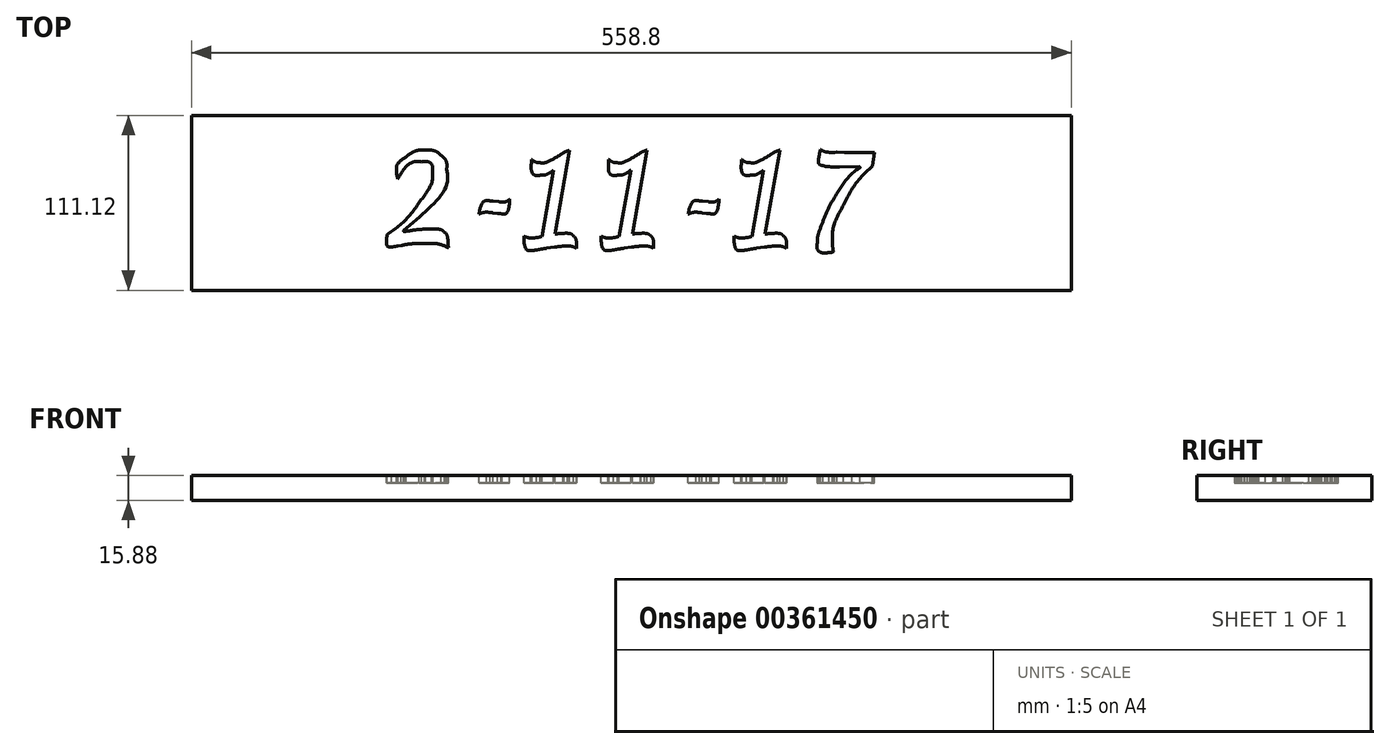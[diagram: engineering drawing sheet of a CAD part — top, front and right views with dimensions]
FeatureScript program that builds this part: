
annotation { "Feature Type Name" : "Feature", "Feature Type Description" : "" }
export const myFeature = defineFeature(function(context is Context, id is Id, definition is map)
    precondition{}
    {
        {
            var Q0;
            Q0=qCreatedBy(makeId("Top.planeOp"),FACE);
            var sketch = newSketch(context, id + "F0", { "sketchPlane" : qUnion([Q0])});
            skLineSegment(sketch, "E0.bottom", {"start": v(12.7, 0) * mm, "end": v(546.1, 0) * mm});
            skLineSegment(sketch, "E0.top", {"start": v(12.7, 609.6) * mm, "end": v(546.1, 609.6) * mm});
            skLineSegment(sketch, "E0.left", {"start": v(0, 12.7) * mm, "end": v(0, 596.9) * mm});
            skLineSegment(sketch, "E0.right", {"start": v(558.8, 12.7) * mm, "end": v(558.8, 596.9) * mm});
            skPoint(sketch, "E1.visualSharp", {"position": v(0, 609.6) * mm});
            skArc(sketch, "E1.filletArc", {"start": v(12.7, 609.6) * mm, "mid": v(3.72, 605.88) * mm, "end": v(0, 596.9) * mm});
            skPoint(sketch, "E2.visualSharp", {"position": v(0, 0) * mm});
            skArc(sketch, "E2.filletArc", {"start": v(0, 12.7) * mm, "mid": v(3.72, 3.72) * mm, "end": v(12.7, 0) * mm});
            skPoint(sketch, "E3.visualSharp", {"position": v(558.8, 0) * mm});
            skArc(sketch, "E3.filletArc", {"start": v(546.1, 0) * mm, "mid": v(555.08, 3.72) * mm, "end": v(558.8, 12.7) * mm});
            skPoint(sketch, "E4.visualSharp", {"position": v(558.8, 609.6) * mm});
            skArc(sketch, "E4.filletArc", {"start": v(558.8, 596.9) * mm, "mid": v(555.08, 605.88) * mm, "end": v(546.1, 609.6) * mm});
            skSolve(sketch);
        }
        {
            var Q0;
            Q0=makeQuery(id+"F0.imprint","IMPRINT",FACE,{"disambiguationData":[TD([[makeQuery(id+"F0.imprint","IMPRINT",EDGE,{"derivedFrom":sQuery(id+"F0.wireOp",EDGE,"E0.bottom")}),1.0]])]});
            extrude(context, id + "F1", {"entities" : qUnion([Q0]), "depth" : 15.88 * mm});
        }
        {
            var Q0;
            Q0=makeQuery(id+"F1.opExtrude","CAP_FACE",FACE,{"disambiguationData":[OSD([sQuery(id+"F0.wireOp",EDGE,"E0.bottom"),sQuery(id+"F0.wireOp",EDGE,"E0.top"),sQuery(id+"F0.wireOp",EDGE,"E0.left"),sQuery(id+"F0.wireOp",EDGE,"E0.right"),sQuery(id+"F0.wireOp",EDGE,"E1.filletArc"),sQuery(id+"F0.wireOp",EDGE,"E2.filletArc"),sQuery(id+"F0.wireOp",EDGE,"E3.filletArc"),sQuery(id+"F0.wireOp",EDGE,"E4.filletArc")])],"isStart":false});
            var sketch = newSketch(context, id + "F2", { "sketchPlane" : qUnion([Q0])});
            skFitSpline(sketch, "E5", {"points": [v(247.46, 485.02) * mm, v(244.22, 485.02) * mm, v(241.38, 482.73) * mm, v(238.94, 478.15) * mm]});
            skFitSpline(sketch, "E6", {"points": [v(238.94, 478.15) * mm, v(236.48, 473.56) * mm, v(235.26, 468.05) * mm, v(235.26, 461.6) * mm]});
            skFitSpline(sketch, "E7", {"points": [v(235.26, 461.6) * mm, v(235.26, 456.87) * mm, v(236.54, 454.5) * mm, v(239.12, 454.5) * mm]});
            skFitSpline(sketch, "E8", {"points": [v(239.12, 454.5) * mm, v(242.2, 454.5) * mm, v(248.34, 462.57) * mm, v(257.6, 478.7) * mm]});
            skFitSpline(sketch, "E9", {"points": [v(257.6, 478.7) * mm, v(257.73, 478.94) * mm, v(258.18, 479.46) * mm, v(258.91, 480.26) * mm]});
            skFitSpline(sketch, "E10", {"points": [v(258.91, 480.26) * mm, v(254.36, 483.44) * mm, v(250.54, 485.02) * mm, v(247.46, 485.02) * mm]});
            skFitSpline(sketch, "E11", {"points": [v(371.38, 485.98) * mm, v(368.47, 485.98) * mm, v(365.74, 484.16) * mm, v(363.18, 480.52) * mm]});
            skFitSpline(sketch, "E12", {"points": [v(363.18, 480.52) * mm, v(360.62, 476.88) * mm, v(359.03, 472.72) * mm, v(358.4, 468.06) * mm]});
            skFitSpline(sketch, "E13", {"points": [v(358.4, 468.06) * mm, v(362.59, 468.32) * mm, v(366.35, 469.82) * mm, v(369.66, 472.53) * mm]});
            skFitSpline(sketch, "E14", {"points": [v(369.66, 472.53) * mm, v(372.98, 475.24) * mm, v(374.64, 478.32) * mm, v(374.64, 481.78) * mm]});
            skFitSpline(sketch, "E15", {"points": [v(374.64, 481.78) * mm, v(374.64, 484.58) * mm, v(373.55, 485.98) * mm, v(371.38, 485.98) * mm]});
            skFitSpline(sketch, "E16", {"points": [v(372.25, 491.45) * mm, v(375.43, 491.45) * mm, v(378, 490.53) * mm, v(379.95, 488.68) * mm]});
            skFitSpline(sketch, "E17", {"points": [v(379.95, 488.68) * mm, v(381.9, 486.84) * mm, v(382.89, 484.38) * mm, v(382.89, 481.3) * mm]});
            skFitSpline(sketch, "E18", {"points": [v(382.89, 481.3) * mm, v(382.89, 476.36) * mm, v(380.3, 472.02) * mm, v(375.12, 468.3) * mm]});
            skFitSpline(sketch, "E19", {"points": [v(375.12, 468.3) * mm, v(369.94, 464.57) * mm, v(364.27, 462.7) * mm, v(358.12, 462.7) * mm]});
            skFitSpline(sketch, "E20", {"points": [v(358.12, 462.7) * mm, v(358.12, 456.15) * mm, v(360.76, 452.87) * mm, v(366.01, 452.87) * mm]});
            skFitSpline(sketch, "E21", {"points": [v(366.01, 452.87) * mm, v(370.84, 452.87) * mm, v(376.2, 455.49) * mm, v(382.13, 460.74) * mm]});
            skFitSpline(sketch, "E22", {"points": [v(382.13, 460.74) * mm, v(388.04, 465.98) * mm, v(393.52, 473.06) * mm, v(398.54, 481.95) * mm]});
            skFitSpline(sketch, "E23", {"points": [v(402.5, 479.62) * mm, v(397.84, 469.55) * mm, v(391.82, 461.33) * mm, v(384.42, 454.98) * mm]});
            skFitSpline(sketch, "E24", {"points": [v(384.42, 454.98) * mm, v(377.03, 448.62) * mm, v(369.98, 445.45) * mm, v(363.3, 445.45) * mm]});
            skFitSpline(sketch, "E25", {"points": [v(363.3, 445.45) * mm, v(358.9, 445.45) * mm, v(355.42, 447.05) * mm, v(352.87, 450.22) * mm]});
            skFitSpline(sketch, "E26", {"points": [v(352.87, 450.22) * mm, v(350.64, 453) * mm, v(349.4, 456.61) * mm, v(349.1, 461.08) * mm]});
            skFitSpline(sketch, "E27", {"points": [v(349.1, 461.08) * mm, v(347.32, 458.56) * mm, v(345.51, 456.33) * mm, v(343.7, 454.35) * mm]});
            skFitSpline(sketch, "E28", {"points": [v(343.7, 454.35) * mm, v(338.24, 448.42) * mm, v(333.27, 445.45) * mm, v(328.8, 445.45) * mm]});
            skFitSpline(sketch, "E29", {"points": [v(328.8, 445.45) * mm, v(325.99, 445.45) * mm, v(323.71, 446.48) * mm, v(322, 448.54) * mm]});
            skFitSpline(sketch, "E30", {"points": [v(322, 448.54) * mm, v(320.27, 450.6) * mm, v(319.41, 453.3) * mm, v(319.41, 456.62) * mm]});
            skFitSpline(sketch, "E31", {"points": [v(319.41, 456.62) * mm, v(319.41, 457.85) * mm, v(319.64, 459.77) * mm, v(320.12, 462.36) * mm]});
            skLineSegment(sketch, "E32", {"start": v(398.54, 481.95) * mm, "end": v(402.5, 479.62) * mm});
            skLineSegment(sketch, "E33", {"start": v(402.5, 479.62) * mm, "end": v(398.54, 481.95) * mm});
            skFitSpline(sketch, "E34", {"points": [v(320.89, 466.68) * mm, v(322, 472.85) * mm, v(322.57, 477.15) * mm, v(322.57, 479.6) * mm]});
            skFitSpline(sketch, "E35", {"points": [v(322.57, 479.6) * mm, v(322.57, 480.87) * mm, v(322.18, 482.24) * mm, v(321.4, 483.7) * mm]});
            skFitSpline(sketch, "E36", {"points": [v(321.4, 483.7) * mm, v(324.84, 484.7) * mm, v(326.97, 485.22) * mm, v(327.78, 485.22) * mm]});
            skFitSpline(sketch, "E37", {"points": [v(327.78, 485.22) * mm, v(329.99, 485.22) * mm, v(331.1, 483.6) * mm, v(331.1, 480.35) * mm]});
            skFitSpline(sketch, "E38", {"points": [v(331.1, 480.35) * mm, v(331.1, 478.32) * mm, v(330.76, 475.38) * mm, v(330.07, 471.54) * mm]});
            skLineSegment(sketch, "E39", {"start": v(320.12, 462.36) * mm, "end": v(320.89, 466.68) * mm});
            skLineSegment(sketch, "E40", {"start": v(320.89, 466.68) * mm, "end": v(320.12, 462.36) * mm});
            skFitSpline(sketch, "E41", {"points": [v(328.7, 463.92) * mm, v(328.05, 460.32) * mm, v(327.73, 458) * mm, v(327.73, 456.92) * mm]});
            skFitSpline(sketch, "E42", {"points": [v(327.73, 456.92) * mm, v(327.73, 454.22) * mm, v(328.7, 452.87) * mm, v(330.64, 452.87) * mm]});
            skFitSpline(sketch, "E43", {"points": [v(330.64, 452.87) * mm, v(333.34, 452.87) * mm, v(337.06, 455.56) * mm, v(341.8, 460.93) * mm]});
            skFitSpline(sketch, "E44", {"points": [v(341.8, 460.93) * mm, v(344.6, 464.12) * mm, v(347.4, 467.87) * mm, v(350.2, 472.2) * mm]});
            skFitSpline(sketch, "E45", {"points": [v(350.2, 472.2) * mm, v(351.28, 476.24) * mm, v(353.16, 479.88) * mm, v(355.83, 483.14) * mm]});
            skFitSpline(sketch, "E46", {"points": [v(355.83, 483.14) * mm, v(360.35, 488.68) * mm, v(365.83, 491.45) * mm, v(372.25, 491.45) * mm]});
            skLineSegment(sketch, "E47", {"start": v(330.07, 471.54) * mm, "end": v(328.7, 463.92) * mm});
            skLineSegment(sketch, "E48", {"start": v(328.7, 463.92) * mm, "end": v(330.07, 471.54) * mm});
            skFitSpline(sketch, "E49", {"points": [v(305.1, 507.84) * mm, v(305.33, 507.84) * mm, v(306.14, 507.78) * mm, v(307.5, 507.65) * mm]});
            skFitSpline(sketch, "E50", {"points": [v(307.5, 507.65) * mm, v(305.64, 504.33) * mm, v(303.76, 499.96) * mm, v(301.86, 494.56) * mm]});
            skFitSpline(sketch, "E51", {"points": [v(319.5, 494.56) * mm, v(322.22, 494.56) * mm, v(324.64, 494.92) * mm, v(326.74, 495.67) * mm]});
            skFitSpline(sketch, "E52", {"points": [v(326.74, 495.67) * mm, v(326.87, 497.05) * mm, v(327.2, 498.41) * mm, v(327.69, 499.77) * mm]});
            skLineSegment(sketch, "E53", {"start": v(301.86, 494.56) * mm, "end": v(319.5, 494.56) * mm});
            skLineSegment(sketch, "E54", {"start": v(319.5, 494.56) * mm, "end": v(301.86, 494.56) * mm});
            skFitSpline(sketch, "E55", {"points": [v(328.67, 499.72) * mm, v(330.08, 499.79) * mm, v(332.2, 500.64) * mm, v(335.04, 502.28) * mm]});
            skFitSpline(sketch, "E56", {"points": [v(335.04, 502.28) * mm, v(337.9, 503.93) * mm, v(340.52, 505.68) * mm, v(342.94, 507.52) * mm]});
            skFitSpline(sketch, "E57", {"points": [v(342.94, 507.52) * mm, v(341.85, 503.08) * mm, v(340.03, 500.06) * mm, v(337.5, 498.48) * mm]});
            skFitSpline(sketch, "E58", {"points": [v(337.5, 498.48) * mm, v(333.26, 493.7) * mm, v(330.34, 491.32) * mm, v(328.76, 491.32) * mm]});
            skFitSpline(sketch, "E59", {"points": [v(328.76, 491.32) * mm, v(327.76, 491.32) * mm, v(327.1, 491.79) * mm, v(326.85, 492.72) * mm]});
            skFitSpline(sketch, "E60", {"points": [v(326.85, 492.72) * mm, v(326.33, 491.05) * mm, v(325.73, 489.92) * mm, v(325.02, 489.33) * mm]});
            skFitSpline(sketch, "E61", {"points": [v(325.02, 489.33) * mm, v(323.92, 488.4) * mm, v(321.98, 487.93) * mm, v(319.18, 487.93) * mm]});
            skLineSegment(sketch, "E62", {"start": v(327.69, 499.77) * mm, "end": v(328.67, 499.72) * mm});
            skLineSegment(sketch, "E63", {"start": v(328.67, 499.72) * mm, "end": v(327.69, 499.77) * mm});
            skFitSpline(sketch, "E64", {"points": [v(300.17, 487.93) * mm, v(300.04, 487.44) * mm, v(299.9, 486.92) * mm, v(299.75, 486.38) * mm]});
            skFitSpline(sketch, "E65", {"points": [v(299.75, 486.38) * mm, v(296.99, 475.84) * mm, v(295.6, 467.88) * mm, v(295.6, 462.47) * mm]});
            skFitSpline(sketch, "E66", {"points": [v(295.6, 462.47) * mm, v(295.6, 456.94) * mm, v(297.3, 454.18) * mm, v(300.68, 454.18) * mm]});
            skFitSpline(sketch, "E67", {"points": [v(300.68, 454.18) * mm, v(302.53, 454.18) * mm, v(304.57, 455.1) * mm, v(306.8, 456.9) * mm]});
            skFitSpline(sketch, "E68", {"points": [v(306.8, 456.9) * mm, v(309.05, 458.71) * mm, v(310.85, 460.91) * mm, v(312.2, 463.5) * mm]});
            skFitSpline(sketch, "E69", {"points": [v(312.2, 463.5) * mm, v(313.35, 461.8) * mm, v(313.92, 460.42) * mm, v(313.92, 459.33) * mm]});
            skFitSpline(sketch, "E70", {"points": [v(313.92, 459.33) * mm, v(313.92, 456.5) * mm, v(311.92, 453.5) * mm, v(307.92, 450.28) * mm]});
            skFitSpline(sketch, "E71", {"points": [v(307.92, 450.28) * mm, v(303.9, 447.06) * mm, v(300.24, 445.45) * mm, v(296.9, 445.45) * mm]});
            skFitSpline(sketch, "E72", {"points": [v(296.9, 445.45) * mm, v(293.88, 445.45) * mm, v(291.42, 446.93) * mm, v(289.56, 449.9) * mm]});
            skFitSpline(sketch, "E73", {"points": [v(289.56, 449.9) * mm, v(287.7, 452.87) * mm, v(286.76, 456.65) * mm, v(286.76, 461.23) * mm]});
            skFitSpline(sketch, "E74", {"points": [v(286.76, 461.23) * mm, v(286.76, 462.58) * mm, v(286.84, 464.08) * mm, v(287.02, 465.75) * mm]});
            skFitSpline(sketch, "E75", {"points": [v(287.02, 465.75) * mm, v(284.81, 462.56) * mm, v(282.47, 459.69) * mm, v(280.01, 457.13) * mm]});
            skFitSpline(sketch, "E76", {"points": [v(280.01, 457.13) * mm, v(274.37, 451.28) * mm, v(269.48, 448.36) * mm, v(265.31, 448.36) * mm]});
            skFitSpline(sketch, "E77", {"points": [v(265.31, 448.36) * mm, v(259.81, 448.36) * mm, v(257.07, 453.3) * mm, v(257.07, 463.23) * mm]});
            skFitSpline(sketch, "E78", {"points": [v(257.07, 463.23) * mm, v(257.07, 465.2) * mm, v(257.14, 467.57) * mm, v(257.28, 470.32) * mm]});
            skFitSpline(sketch, "E79", {"points": [v(257.28, 470.32) * mm, v(255.19, 463.64) * mm, v(251.91, 457.83) * mm, v(247.46, 452.87) * mm]});
            skFitSpline(sketch, "E80", {"points": [v(247.46, 452.87) * mm, v(242.99, 447.92) * mm, v(239.04, 445.45) * mm, v(235.6, 445.45) * mm]});
            skFitSpline(sketch, "E81", {"points": [v(235.6, 445.45) * mm, v(232.88, 445.45) * mm, v(230.72, 446.77) * mm, v(229.15, 449.4) * mm]});
            skFitSpline(sketch, "E82", {"points": [v(229.15, 449.4) * mm, v(227.56, 452.05) * mm, v(226.77, 455.51) * mm, v(226.77, 459.78) * mm]});
            skFitSpline(sketch, "E83", {"points": [v(226.77, 459.78) * mm, v(226.77, 468.13) * mm, v(229.03, 475.5) * mm, v(233.56, 481.87) * mm]});
            skFitSpline(sketch, "E84", {"points": [v(233.56, 481.87) * mm, v(238.09, 488.26) * mm, v(243.35, 491.45) * mm, v(249.38, 491.45) * mm]});
            skFitSpline(sketch, "E85", {"points": [v(249.38, 491.45) * mm, v(253.01, 491.45) * mm, v(256.66, 490.21) * mm, v(260.33, 487.76) * mm]});
            skFitSpline(sketch, "E86", {"points": [v(260.33, 487.76) * mm, v(260.86, 490.19) * mm, v(263.48, 491.4) * mm, v(268.16, 491.4) * mm]});
            skFitSpline(sketch, "E87", {"points": [v(268.16, 491.4) * mm, v(268.26, 491.4) * mm, v(268.96, 491.37) * mm, v(270.27, 491.3) * mm]});
            skFitSpline(sketch, "E88", {"points": [v(270.27, 491.3) * mm, v(268.9, 488.33) * mm, v(267.89, 484.93) * mm, v(267.2, 481.1) * mm]});
            skLineSegment(sketch, "E89", {"start": v(319.18, 487.93) * mm, "end": v(300.17, 487.93) * mm});
            skLineSegment(sketch, "E90", {"start": v(300.17, 487.93) * mm, "end": v(319.18, 487.93) * mm});
            skFitSpline(sketch, "E91", {"points": [v(266.62, 477.77) * mm, v(265.96, 474.15) * mm, v(265.63, 469.88) * mm, v(265.63, 464.94) * mm]});
            skFitSpline(sketch, "E92", {"points": [v(265.63, 464.94) * mm, v(265.63, 459.77) * mm, v(266.57, 457.18) * mm, v(268.44, 457.18) * mm]});
            skFitSpline(sketch, "E93", {"points": [v(268.44, 457.18) * mm, v(270.76, 457.18) * mm, v(274.05, 459.48) * mm, v(278.32, 464.1) * mm]});
            skFitSpline(sketch, "E94", {"points": [v(278.32, 464.1) * mm, v(281.96, 468.04) * mm, v(285.66, 473) * mm, v(289.42, 478.98) * mm]});
            skFitSpline(sketch, "E95", {"points": [v(289.42, 478.98) * mm, v(289.7, 480.18) * mm, v(290, 481.4) * mm, v(290.32, 482.69) * mm]});
            skLineSegment(sketch, "E96", {"start": v(267.2, 481.1) * mm, "end": v(266.62, 477.77) * mm});
            skLineSegment(sketch, "E97", {"start": v(266.62, 477.77) * mm, "end": v(267.2, 481.1) * mm});
            skFitSpline(sketch, "E98", {"points": [v(286.65, 487.93) * mm, v(284.3, 487.93) * mm, v(282.1, 487.54) * mm, v(280.04, 486.76) * mm]});
            skFitSpline(sketch, "E99", {"points": [v(280.04, 486.76) * mm, v(281.5, 490.38) * mm, v(282.72, 492.6) * mm, v(283.72, 493.38) * mm]});
            skFitSpline(sketch, "E100", {"points": [v(283.72, 493.38) * mm, v(284.71, 494.16) * mm, v(286.34, 494.56) * mm, v(288.6, 494.56) * mm]});
            skLineSegment(sketch, "E101", {"start": v(290.32, 482.69) * mm, "end": v(291.82, 487.93) * mm});
            skLineSegment(sketch, "E102", {"start": v(291.82, 487.93) * mm, "end": v(286.65, 487.93) * mm});
            skFitSpline(sketch, "E103", {"points": [v(293.99, 497.12) * mm, v(295.02, 501) * mm, v(296.33, 503.76) * mm, v(297.95, 505.4) * mm]});
            skFitSpline(sketch, "E104", {"points": [v(297.95, 505.4) * mm, v(299.55, 507.03) * mm, v(301.94, 507.84) * mm, v(305.1, 507.84) * mm]});
            skLineSegment(sketch, "E105", {"start": v(288.6, 494.56) * mm, "end": v(293.33, 494.56) * mm});
            skLineSegment(sketch, "E106", {"start": v(293.33, 494.56) * mm, "end": v(293.99, 497.12) * mm});
            skFitSpline(sketch, "E107", {"points": [v(178.41, 506.2) * mm, v(181.96, 506.2) * mm, v(186.85, 506.6) * mm, v(193.08, 507.4) * mm]});
            skFitSpline(sketch, "E108", {"points": [v(188.04, 478.85) * mm, v(200.42, 488.81) * mm, v(207.85, 498.44) * mm, v(210.33, 507.7) * mm]});
            skFitSpline(sketch, "E109", {"points": [v(210.33, 507.7) * mm, v(214.42, 505.56) * mm, v(216.46, 503.26) * mm, v(216.46, 500.79) * mm]});
            skFitSpline(sketch, "E110", {"points": [v(216.46, 500.79) * mm, v(216.46, 499.37) * mm, v(213.98, 496.13) * mm, v(209, 491.1) * mm]});
            skFitSpline(sketch, "E111", {"points": [v(209, 491.1) * mm, v(204.02, 486.08) * mm, v(199.1, 481.73) * mm, v(194.23, 478.07) * mm]});
            skFitSpline(sketch, "E112", {"points": [v(194.23, 478.07) * mm, v(198.39, 469.54) * mm, v(202.46, 462.52) * mm, v(206.43, 457.03) * mm]});
            skFitSpline(sketch, "E113", {"points": [v(206.43, 457.03) * mm, v(210.4, 451.54) * mm, v(213.38, 448.8) * mm, v(215.37, 448.8) * mm]});
            skFitSpline(sketch, "E114", {"points": [v(215.37, 448.8) * mm, v(217.55, 448.8) * mm, v(220.39, 450.27) * mm, v(223.87, 453.22) * mm]});
            skLineSegment(sketch, "E115", {"start": v(193.08, 507.4) * mm, "end": v(188.04, 478.85) * mm});
            skLineSegment(sketch, "E116", {"start": v(188.04, 478.85) * mm, "end": v(193.08, 507.4) * mm});
            skFitSpline(sketch, "E117", {"points": [v(223.98, 451.1) * mm, v(223.98, 449.09) * mm, v(222.68, 446.98) * mm, v(220.08, 444.73) * mm]});
            skFitSpline(sketch, "E118", {"points": [v(220.08, 444.73) * mm, v(217.49, 442.5) * mm, v(214.96, 441.38) * mm, v(212.51, 441.38) * mm]});
            skFitSpline(sketch, "E119", {"points": [v(212.51, 441.38) * mm, v(206.3, 441.38) * mm, v(197.85, 452.5) * mm, v(187.18, 474.76) * mm]});
            skLineSegment(sketch, "E120", {"start": v(223.87, 453.22) * mm, "end": v(223.98, 451.1) * mm});
            skLineSegment(sketch, "E121", {"start": v(223.98, 451.1) * mm, "end": v(223.87, 453.22) * mm});
            skFitSpline(sketch, "E122", {"points": [v(183.9, 454.8) * mm, v(183.48, 452.44) * mm, v(183.27, 450.88) * mm, v(183.27, 450.14) * mm]});
            skFitSpline(sketch, "E123", {"points": [v(183.27, 450.14) * mm, v(183.27, 449.5) * mm, v(183.42, 448.6) * mm, v(183.73, 447.42) * mm]});
            skFitSpline(sketch, "E124", {"points": [v(183.73, 447.42) * mm, v(180.96, 445.82) * mm, v(178.55, 445.01) * mm, v(176.52, 445.01) * mm]});
            skFitSpline(sketch, "E125", {"points": [v(176.52, 445.01) * mm, v(174.84, 445.01) * mm, v(174, 445.83) * mm, v(174, 447.45) * mm]});
            skFitSpline(sketch, "E126", {"points": [v(174, 447.45) * mm, v(174, 448.08) * mm, v(174.25, 449.8) * mm, v(174.74, 452.56) * mm]});
            skLineSegment(sketch, "E127", {"start": v(187.18, 474.76) * mm, "end": v(183.9, 454.8) * mm});
            skLineSegment(sketch, "E128", {"start": v(183.9, 454.8) * mm, "end": v(187.18, 474.76) * mm});
            skFitSpline(sketch, "E129", {"points": [v(183.17, 499.25) * mm, v(181.66, 498.94) * mm, v(180, 498.79) * mm, v(178.17, 498.79) * mm]});
            skFitSpline(sketch, "E130", {"points": [v(178.17, 498.79) * mm, v(174.1, 498.79) * mm, v(171.7, 502.02) * mm, v(170.94, 508.51) * mm]});
            skLineSegment(sketch, "E131", {"start": v(174.74, 452.56) * mm, "end": v(183.17, 499.25) * mm});
            skLineSegment(sketch, "E132", {"start": v(183.17, 499.25) * mm, "end": v(174.74, 452.56) * mm});
            skFitSpline(sketch, "E133", {"points": [v(247.46, 485.02) * mm, v(244.22, 485.02) * mm, v(241.38, 482.73) * mm, v(238.94, 478.15) * mm]});
            skFitSpline(sketch, "E134", {"points": [v(238.94, 478.15) * mm, v(236.48, 473.56) * mm, v(235.26, 468.05) * mm, v(235.26, 461.6) * mm]});
            skFitSpline(sketch, "E135", {"points": [v(235.26, 461.6) * mm, v(235.26, 456.87) * mm, v(236.54, 454.5) * mm, v(239.12, 454.5) * mm]});
            skFitSpline(sketch, "E136", {"points": [v(239.12, 454.5) * mm, v(242.2, 454.5) * mm, v(248.34, 462.57) * mm, v(257.6, 478.7) * mm]});
            skFitSpline(sketch, "E137", {"points": [v(257.6, 478.7) * mm, v(257.73, 478.94) * mm, v(258.18, 479.46) * mm, v(258.91, 480.26) * mm]});
            skFitSpline(sketch, "E138", {"points": [v(258.91, 480.26) * mm, v(254.36, 483.44) * mm, v(250.54, 485.02) * mm, v(247.46, 485.02) * mm]});
            skFitSpline(sketch, "E139", {"points": [v(371.38, 485.98) * mm, v(368.47, 485.98) * mm, v(365.74, 484.16) * mm, v(363.18, 480.52) * mm]});
            skFitSpline(sketch, "E140", {"points": [v(363.18, 480.52) * mm, v(360.62, 476.88) * mm, v(359.03, 472.72) * mm, v(358.4, 468.06) * mm]});
            skFitSpline(sketch, "E141", {"points": [v(358.4, 468.06) * mm, v(362.59, 468.32) * mm, v(366.35, 469.82) * mm, v(369.66, 472.53) * mm]});
            skFitSpline(sketch, "E142", {"points": [v(369.66, 472.53) * mm, v(372.98, 475.24) * mm, v(374.64, 478.32) * mm, v(374.64, 481.78) * mm]});
            skFitSpline(sketch, "E143", {"points": [v(374.64, 481.78) * mm, v(374.64, 484.58) * mm, v(373.55, 485.98) * mm, v(371.38, 485.98) * mm]});
            skFitSpline(sketch, "E144", {"points": [v(372.25, 491.45) * mm, v(375.43, 491.45) * mm, v(378, 490.53) * mm, v(379.95, 488.68) * mm]});
            skFitSpline(sketch, "E145", {"points": [v(379.95, 488.68) * mm, v(381.9, 486.84) * mm, v(382.89, 484.38) * mm, v(382.89, 481.3) * mm]});
            skFitSpline(sketch, "E146", {"points": [v(382.89, 481.3) * mm, v(382.89, 476.36) * mm, v(380.3, 472.02) * mm, v(375.12, 468.3) * mm]});
            skFitSpline(sketch, "E147", {"points": [v(375.12, 468.3) * mm, v(369.94, 464.57) * mm, v(364.27, 462.7) * mm, v(358.12, 462.7) * mm]});
            skFitSpline(sketch, "E148", {"points": [v(358.12, 462.7) * mm, v(358.12, 456.15) * mm, v(360.76, 452.87) * mm, v(366.01, 452.87) * mm]});
            skFitSpline(sketch, "E149", {"points": [v(366.01, 452.87) * mm, v(370.84, 452.87) * mm, v(376.2, 455.49) * mm, v(382.13, 460.74) * mm]});
            skFitSpline(sketch, "E150", {"points": [v(382.13, 460.74) * mm, v(388.04, 465.98) * mm, v(393.52, 473.06) * mm, v(398.54, 481.95) * mm]});
            skFitSpline(sketch, "E151", {"points": [v(402.5, 479.62) * mm, v(397.84, 469.55) * mm, v(391.82, 461.33) * mm, v(384.42, 454.98) * mm]});
            skFitSpline(sketch, "E152", {"points": [v(384.42, 454.98) * mm, v(377.03, 448.62) * mm, v(369.98, 445.45) * mm, v(363.3, 445.45) * mm]});
            skFitSpline(sketch, "E153", {"points": [v(363.3, 445.45) * mm, v(358.9, 445.45) * mm, v(355.42, 447.05) * mm, v(352.87, 450.22) * mm]});
            skFitSpline(sketch, "E154", {"points": [v(352.87, 450.22) * mm, v(350.64, 453) * mm, v(349.4, 456.61) * mm, v(349.1, 461.08) * mm]});
            skFitSpline(sketch, "E155", {"points": [v(349.1, 461.08) * mm, v(347.32, 458.56) * mm, v(345.51, 456.33) * mm, v(343.7, 454.35) * mm]});
            skFitSpline(sketch, "E156", {"points": [v(343.7, 454.35) * mm, v(338.24, 448.42) * mm, v(333.27, 445.45) * mm, v(328.8, 445.45) * mm]});
            skFitSpline(sketch, "E157", {"points": [v(328.8, 445.45) * mm, v(325.99, 445.45) * mm, v(323.71, 446.48) * mm, v(322, 448.54) * mm]});
            skFitSpline(sketch, "E158", {"points": [v(322, 448.54) * mm, v(320.27, 450.6) * mm, v(319.41, 453.3) * mm, v(319.41, 456.62) * mm]});
            skFitSpline(sketch, "E159", {"points": [v(319.41, 456.62) * mm, v(319.41, 457.85) * mm, v(319.64, 459.77) * mm, v(320.12, 462.36) * mm]});
            skFitSpline(sketch, "E160", {"points": [v(320.89, 466.68) * mm, v(322, 472.85) * mm, v(322.57, 477.15) * mm, v(322.57, 479.6) * mm]});
            skFitSpline(sketch, "E161", {"points": [v(322.57, 479.6) * mm, v(322.57, 480.87) * mm, v(322.18, 482.24) * mm, v(321.4, 483.7) * mm]});
            skFitSpline(sketch, "E162", {"points": [v(321.4, 483.7) * mm, v(324.84, 484.7) * mm, v(326.97, 485.22) * mm, v(327.78, 485.22) * mm]});
            skFitSpline(sketch, "E163", {"points": [v(327.78, 485.22) * mm, v(329.99, 485.22) * mm, v(331.1, 483.6) * mm, v(331.1, 480.35) * mm]});
            skFitSpline(sketch, "E164", {"points": [v(331.1, 480.35) * mm, v(331.1, 478.32) * mm, v(330.76, 475.38) * mm, v(330.07, 471.54) * mm]});
            skFitSpline(sketch, "E165", {"points": [v(328.7, 463.92) * mm, v(328.05, 460.32) * mm, v(327.73, 458) * mm, v(327.73, 456.92) * mm]});
            skFitSpline(sketch, "E166", {"points": [v(327.73, 456.92) * mm, v(327.73, 454.22) * mm, v(328.7, 452.87) * mm, v(330.64, 452.87) * mm]});
            skFitSpline(sketch, "E167", {"points": [v(330.64, 452.87) * mm, v(333.34, 452.87) * mm, v(337.06, 455.56) * mm, v(341.8, 460.93) * mm]});
            skFitSpline(sketch, "E168", {"points": [v(341.8, 460.93) * mm, v(344.6, 464.12) * mm, v(347.4, 467.87) * mm, v(350.2, 472.2) * mm]});
            skFitSpline(sketch, "E169", {"points": [v(350.2, 472.2) * mm, v(351.28, 476.24) * mm, v(353.16, 479.88) * mm, v(355.83, 483.14) * mm]});
            skFitSpline(sketch, "E170", {"points": [v(355.83, 483.14) * mm, v(360.35, 488.68) * mm, v(365.83, 491.45) * mm, v(372.25, 491.45) * mm]});
            skFitSpline(sketch, "E171", {"points": [v(305.1, 507.84) * mm, v(305.33, 507.84) * mm, v(306.14, 507.78) * mm, v(307.5, 507.65) * mm]});
            skFitSpline(sketch, "E172", {"points": [v(307.5, 507.65) * mm, v(305.64, 504.33) * mm, v(303.76, 499.96) * mm, v(301.86, 494.56) * mm]});
            skFitSpline(sketch, "E173", {"points": [v(319.5, 494.56) * mm, v(322.22, 494.56) * mm, v(324.64, 494.92) * mm, v(326.74, 495.67) * mm]});
            skFitSpline(sketch, "E174", {"points": [v(326.74, 495.67) * mm, v(326.87, 497.05) * mm, v(327.2, 498.41) * mm, v(327.69, 499.77) * mm]});
            skFitSpline(sketch, "E175", {"points": [v(328.67, 499.72) * mm, v(330.08, 499.79) * mm, v(332.2, 500.64) * mm, v(335.04, 502.28) * mm]});
            skFitSpline(sketch, "E176", {"points": [v(335.04, 502.28) * mm, v(337.9, 503.93) * mm, v(340.52, 505.68) * mm, v(342.94, 507.52) * mm]});
            skFitSpline(sketch, "E177", {"points": [v(342.94, 507.52) * mm, v(341.85, 503.08) * mm, v(340.03, 500.06) * mm, v(337.5, 498.48) * mm]});
            skFitSpline(sketch, "E178", {"points": [v(337.5, 498.48) * mm, v(333.26, 493.7) * mm, v(330.34, 491.32) * mm, v(328.76, 491.32) * mm]});
            skFitSpline(sketch, "E179", {"points": [v(328.76, 491.32) * mm, v(327.76, 491.32) * mm, v(327.1, 491.79) * mm, v(326.85, 492.72) * mm]});
            skFitSpline(sketch, "E180", {"points": [v(326.85, 492.72) * mm, v(326.33, 491.05) * mm, v(325.73, 489.92) * mm, v(325.02, 489.33) * mm]});
            skFitSpline(sketch, "E181", {"points": [v(325.02, 489.33) * mm, v(323.92, 488.4) * mm, v(321.98, 487.93) * mm, v(319.18, 487.93) * mm]});
            skFitSpline(sketch, "E182", {"points": [v(300.17, 487.93) * mm, v(300.04, 487.44) * mm, v(299.9, 486.92) * mm, v(299.75, 486.38) * mm]});
            skFitSpline(sketch, "E183", {"points": [v(299.75, 486.38) * mm, v(296.99, 475.84) * mm, v(295.6, 467.88) * mm, v(295.6, 462.47) * mm]});
            skFitSpline(sketch, "E184", {"points": [v(295.6, 462.47) * mm, v(295.6, 456.94) * mm, v(297.3, 454.18) * mm, v(300.68, 454.18) * mm]});
            skFitSpline(sketch, "E185", {"points": [v(300.68, 454.18) * mm, v(302.53, 454.18) * mm, v(304.57, 455.1) * mm, v(306.8, 456.9) * mm]});
            skFitSpline(sketch, "E186", {"points": [v(306.8, 456.9) * mm, v(309.05, 458.71) * mm, v(310.85, 460.91) * mm, v(312.2, 463.5) * mm]});
            skFitSpline(sketch, "E187", {"points": [v(312.2, 463.5) * mm, v(313.35, 461.8) * mm, v(313.92, 460.42) * mm, v(313.92, 459.33) * mm]});
            skFitSpline(sketch, "E188", {"points": [v(313.92, 459.33) * mm, v(313.92, 456.5) * mm, v(311.92, 453.5) * mm, v(307.92, 450.28) * mm]});
            skFitSpline(sketch, "E189", {"points": [v(307.92, 450.28) * mm, v(303.9, 447.06) * mm, v(300.24, 445.45) * mm, v(296.9, 445.45) * mm]});
            skFitSpline(sketch, "E190", {"points": [v(296.9, 445.45) * mm, v(293.88, 445.45) * mm, v(291.42, 446.93) * mm, v(289.56, 449.9) * mm]});
            skFitSpline(sketch, "E191", {"points": [v(289.56, 449.9) * mm, v(287.7, 452.87) * mm, v(286.76, 456.65) * mm, v(286.76, 461.23) * mm]});
            skFitSpline(sketch, "E192", {"points": [v(286.76, 461.23) * mm, v(286.76, 462.58) * mm, v(286.84, 464.08) * mm, v(287.02, 465.75) * mm]});
            skFitSpline(sketch, "E193", {"points": [v(287.02, 465.75) * mm, v(284.81, 462.56) * mm, v(282.47, 459.69) * mm, v(280.01, 457.13) * mm]});
            skFitSpline(sketch, "E194", {"points": [v(280.01, 457.13) * mm, v(274.37, 451.28) * mm, v(269.48, 448.36) * mm, v(265.31, 448.36) * mm]});
            skFitSpline(sketch, "E195", {"points": [v(265.31, 448.36) * mm, v(259.81, 448.36) * mm, v(257.07, 453.3) * mm, v(257.07, 463.23) * mm]});
            skFitSpline(sketch, "E196", {"points": [v(257.07, 463.23) * mm, v(257.07, 465.2) * mm, v(257.14, 467.57) * mm, v(257.28, 470.32) * mm]});
            skFitSpline(sketch, "E197", {"points": [v(257.28, 470.32) * mm, v(255.19, 463.64) * mm, v(251.91, 457.83) * mm, v(247.46, 452.87) * mm]});
            skFitSpline(sketch, "E198", {"points": [v(247.46, 452.87) * mm, v(242.99, 447.92) * mm, v(239.04, 445.45) * mm, v(235.6, 445.45) * mm]});
            skFitSpline(sketch, "E199", {"points": [v(235.6, 445.45) * mm, v(232.88, 445.45) * mm, v(230.72, 446.77) * mm, v(229.15, 449.4) * mm]});
            skFitSpline(sketch, "E200", {"points": [v(229.15, 449.4) * mm, v(227.56, 452.05) * mm, v(226.77, 455.51) * mm, v(226.77, 459.78) * mm]});
            skFitSpline(sketch, "E201", {"points": [v(226.77, 459.78) * mm, v(226.77, 468.13) * mm, v(229.03, 475.5) * mm, v(233.56, 481.87) * mm]});
            skFitSpline(sketch, "E202", {"points": [v(233.56, 481.87) * mm, v(238.09, 488.26) * mm, v(243.35, 491.45) * mm, v(249.38, 491.45) * mm]});
            skFitSpline(sketch, "E203", {"points": [v(249.38, 491.45) * mm, v(253.01, 491.45) * mm, v(256.66, 490.21) * mm, v(260.33, 487.76) * mm]});
            skFitSpline(sketch, "E204", {"points": [v(260.33, 487.76) * mm, v(260.86, 490.19) * mm, v(263.48, 491.4) * mm, v(268.16, 491.4) * mm]});
            skFitSpline(sketch, "E205", {"points": [v(268.16, 491.4) * mm, v(268.26, 491.4) * mm, v(268.96, 491.37) * mm, v(270.27, 491.3) * mm]});
            skFitSpline(sketch, "E206", {"points": [v(270.27, 491.3) * mm, v(268.9, 488.33) * mm, v(267.89, 484.93) * mm, v(267.2, 481.1) * mm]});
            skFitSpline(sketch, "E207", {"points": [v(266.62, 477.77) * mm, v(265.96, 474.15) * mm, v(265.63, 469.88) * mm, v(265.63, 464.94) * mm]});
            skFitSpline(sketch, "E208", {"points": [v(265.63, 464.94) * mm, v(265.63, 459.77) * mm, v(266.57, 457.18) * mm, v(268.44, 457.18) * mm]});
            skFitSpline(sketch, "E209", {"points": [v(268.44, 457.18) * mm, v(270.76, 457.18) * mm, v(274.05, 459.48) * mm, v(278.32, 464.1) * mm]});
            skFitSpline(sketch, "E210", {"points": [v(278.32, 464.1) * mm, v(281.96, 468.04) * mm, v(285.66, 473) * mm, v(289.42, 478.98) * mm]});
            skFitSpline(sketch, "E211", {"points": [v(289.42, 478.98) * mm, v(289.7, 480.18) * mm, v(290, 481.4) * mm, v(290.32, 482.69) * mm]});
            skFitSpline(sketch, "E212", {"points": [v(286.65, 487.93) * mm, v(284.3, 487.93) * mm, v(282.1, 487.54) * mm, v(280.04, 486.76) * mm]});
            skFitSpline(sketch, "E213", {"points": [v(280.04, 486.76) * mm, v(281.5, 490.38) * mm, v(282.72, 492.6) * mm, v(283.72, 493.38) * mm]});
            skFitSpline(sketch, "E214", {"points": [v(283.72, 493.38) * mm, v(284.71, 494.16) * mm, v(286.34, 494.56) * mm, v(288.6, 494.56) * mm]});
            skFitSpline(sketch, "E215", {"points": [v(293.99, 497.12) * mm, v(295.02, 501) * mm, v(296.33, 503.76) * mm, v(297.95, 505.4) * mm]});
            skFitSpline(sketch, "E216", {"points": [v(297.95, 505.4) * mm, v(299.55, 507.03) * mm, v(301.94, 507.84) * mm, v(305.1, 507.84) * mm]});
            skFitSpline(sketch, "E217", {"points": [v(170.94, 508.51) * mm, v(173.27, 506.97) * mm, v(175.75, 506.2) * mm, v(178.41, 506.2) * mm]});
            skFitSpline(sketch, "E218", {"points": [v(178.41, 506.2) * mm, v(181.96, 506.2) * mm, v(186.85, 506.6) * mm, v(193.08, 507.4) * mm]});
            skFitSpline(sketch, "E219", {"points": [v(188.04, 478.85) * mm, v(200.42, 488.81) * mm, v(207.85, 498.44) * mm, v(210.33, 507.7) * mm]});
            skFitSpline(sketch, "E220", {"points": [v(210.33, 507.7) * mm, v(214.42, 505.56) * mm, v(216.46, 503.26) * mm, v(216.46, 500.79) * mm]});
            skFitSpline(sketch, "E221", {"points": [v(216.46, 500.79) * mm, v(216.46, 499.37) * mm, v(213.98, 496.13) * mm, v(209, 491.1) * mm]});
            skFitSpline(sketch, "E222", {"points": [v(209, 491.1) * mm, v(204.02, 486.08) * mm, v(199.1, 481.73) * mm, v(194.23, 478.07) * mm]});
            skFitSpline(sketch, "E223", {"points": [v(194.23, 478.07) * mm, v(198.39, 469.54) * mm, v(202.46, 462.52) * mm, v(206.43, 457.03) * mm]});
            skFitSpline(sketch, "E224", {"points": [v(206.43, 457.03) * mm, v(210.4, 451.54) * mm, v(213.38, 448.8) * mm, v(215.37, 448.8) * mm]});
            skFitSpline(sketch, "E225", {"points": [v(215.37, 448.8) * mm, v(217.55, 448.8) * mm, v(220.39, 450.27) * mm, v(223.87, 453.22) * mm]});
            skFitSpline(sketch, "E226", {"points": [v(223.98, 451.1) * mm, v(223.98, 449.09) * mm, v(222.68, 446.98) * mm, v(220.08, 444.73) * mm]});
            skFitSpline(sketch, "E227", {"points": [v(220.08, 444.73) * mm, v(217.49, 442.5) * mm, v(214.96, 441.38) * mm, v(212.51, 441.38) * mm]});
            skFitSpline(sketch, "E228", {"points": [v(212.51, 441.38) * mm, v(206.3, 441.38) * mm, v(197.85, 452.5) * mm, v(187.18, 474.76) * mm]});
            skFitSpline(sketch, "E229", {"points": [v(183.9, 454.8) * mm, v(183.48, 452.44) * mm, v(183.27, 450.88) * mm, v(183.27, 450.14) * mm]});
            skFitSpline(sketch, "E230", {"points": [v(183.27, 450.14) * mm, v(183.27, 449.5) * mm, v(183.42, 448.6) * mm, v(183.73, 447.42) * mm]});
            skFitSpline(sketch, "E231", {"points": [v(183.73, 447.42) * mm, v(180.96, 445.82) * mm, v(178.55, 445.01) * mm, v(176.52, 445.01) * mm]});
            skFitSpline(sketch, "E232", {"points": [v(176.52, 445.01) * mm, v(174.84, 445.01) * mm, v(174, 445.83) * mm, v(174, 447.45) * mm]});
            skFitSpline(sketch, "E233", {"points": [v(174, 447.45) * mm, v(174, 448.08) * mm, v(174.25, 449.8) * mm, v(174.74, 452.56) * mm]});
            skFitSpline(sketch, "E234", {"points": [v(183.17, 499.25) * mm, v(181.66, 498.94) * mm, v(180, 498.79) * mm, v(178.17, 498.79) * mm]});
            skFitSpline(sketch, "E235", {"points": [v(178.17, 498.79) * mm, v(174.1, 498.79) * mm, v(171.7, 502.02) * mm, v(170.94, 508.51) * mm]});
            skFitSpline(sketch, "E236", {"points": [v(277.79, 394.65) * mm, v(280.95, 394.65) * mm, v(283.67, 394.04) * mm, v(285.93, 392.83) * mm]});
            skFitSpline(sketch, "E237", {"points": [v(285.93, 392.83) * mm, v(288.2, 391.61) * mm, v(289.33, 390.05) * mm, v(289.33, 388.1) * mm]});
            skFitSpline(sketch, "E238", {"points": [v(289.33, 388.1) * mm, v(289.33, 386.55) * mm, v(288.3, 384.9) * mm, v(286.28, 383.13) * mm]});
            skFitSpline(sketch, "E239", {"points": [v(286.28, 383.13) * mm, v(284.16, 387.16) * mm, v(281.01, 389.18) * mm, v(276.84, 389.18) * mm]});
            skFitSpline(sketch, "E240", {"points": [v(276.84, 389.18) * mm, v(274.08, 389.18) * mm, v(271.82, 388.38) * mm, v(270.07, 386.75) * mm]});
            skFitSpline(sketch, "E241", {"points": [v(270.07, 386.75) * mm, v(268.32, 385.12) * mm, v(267.44, 383.06) * mm, v(267.44, 380.56) * mm]});
            skFitSpline(sketch, "E242", {"points": [v(267.44, 380.56) * mm, v(267.44, 377.66) * mm, v(268.8, 375.02) * mm, v(271.5, 372.69) * mm]});
            skFitSpline(sketch, "E243", {"points": [v(271.5, 372.69) * mm, v(273.4, 373.18) * mm, v(275.11, 373.43) * mm, v(276.63, 373.43) * mm]});
            skFitSpline(sketch, "E244", {"points": [v(276.63, 373.43) * mm, v(278.07, 373.43) * mm, v(279.73, 373.08) * mm, v(281.63, 372.4) * mm]});
            skFitSpline(sketch, "E245", {"points": [v(281.63, 372.4) * mm, v(280.16, 367.34) * mm, v(277.58, 364.81) * mm, v(273.88, 364.81) * mm]});
            skFitSpline(sketch, "E246", {"points": [v(273.88, 364.81) * mm, v(272.36, 364.81) * mm, v(270.86, 365.22) * mm, v(269.35, 366.02) * mm]});
            skFitSpline(sketch, "E247", {"points": [v(269.35, 366.02) * mm, v(265.7, 364.5) * mm, v(262.72, 362.19) * mm, v(260.42, 359.13) * mm]});
            skFitSpline(sketch, "E248", {"points": [v(260.42, 359.13) * mm, v(258.12, 356.06) * mm, v(256.96, 352.8) * mm, v(256.96, 349.32) * mm]});
            skFitSpline(sketch, "E249", {"points": [v(256.96, 349.32) * mm, v(256.96, 346.25) * mm, v(258.1, 343.74) * mm, v(260.39, 341.8) * mm]});
            skFitSpline(sketch, "E250", {"points": [v(260.39, 341.8) * mm, v(262.67, 339.86) * mm, v(265.66, 338.88) * mm, v(269.4, 338.88) * mm]});
            skFitSpline(sketch, "E251", {"points": [v(269.4, 338.88) * mm, v(273.9, 338.88) * mm, v(278.46, 340.78) * mm, v(283.03, 344.56) * mm]});
            skFitSpline(sketch, "E252", {"points": [v(283.03, 344.56) * mm, v(287.61, 348.33) * mm, v(289.9, 352.03) * mm, v(289.9, 355.63) * mm]});
            skFitSpline(sketch, "E253", {"points": [v(289.9, 355.63) * mm, v(289.9, 357.33) * mm, v(289.16, 358.57) * mm, v(287.7, 359.33) * mm]});
            skFitSpline(sketch, "E254", {"points": [v(286.49, 359.8) * mm, v(285.1, 360.5) * mm, v(284.39, 361.54) * mm, v(284.39, 362.92) * mm]});
            skFitSpline(sketch, "E255", {"points": [v(284.39, 362.92) * mm, v(284.39, 364.24) * mm, v(284.98, 366.15) * mm, v(286.17, 368.6) * mm]});
            skFitSpline(sketch, "E256", {"points": [v(286.17, 368.6) * mm, v(289.42, 367.14) * mm, v(293.87, 366.41) * mm, v(299.52, 366.41) * mm]});
            skFitSpline(sketch, "E257", {"points": [v(299.52, 366.41) * mm, v(302.52, 366.41) * mm, v(305.82, 366.82) * mm, v(309.44, 367.62) * mm]});
            skFitSpline(sketch, "E258", {"points": [v(309.44, 367.62) * mm, v(308.5, 363.93) * mm, v(307.32, 361.5) * mm, v(305.9, 360.33) * mm]});
            skFitSpline(sketch, "E259", {"points": [v(305.9, 360.33) * mm, v(304.46, 359.17) * mm, v(302.3, 358.6) * mm, v(299.4, 358.6) * mm]});
            skFitSpline(sketch, "E260", {"points": [v(299.4, 358.6) * mm, v(298.84, 358.6) * mm, v(298.17, 358.64) * mm, v(297.4, 358.75) * mm]});
            skFitSpline(sketch, "E261", {"points": [v(297.4, 358.75) * mm, v(294.74, 350.17) * mm, v(293.41, 343.18) * mm, v(293.41, 337.77) * mm]});
            skFitSpline(sketch, "E262", {"points": [v(293.41, 337.77) * mm, v(293.41, 333.72) * mm, v(294.08, 330.44) * mm, v(295.4, 327.95) * mm]});
            skFitSpline(sketch, "E263", {"points": [v(295.4, 327.95) * mm, v(293.52, 325.82) * mm, v(291.53, 324.77) * mm, v(289.43, 324.77) * mm]});
            skFitSpline(sketch, "E264", {"points": [v(289.43, 324.77) * mm, v(287.44, 324.77) * mm, v(286.45, 326.37) * mm, v(286.45, 329.58) * mm]});
            skFitSpline(sketch, "E265", {"points": [v(286.45, 329.58) * mm, v(286.45, 332.7) * mm, v(287.06, 337.43) * mm, v(288.26, 343.75) * mm]});
            skFitSpline(sketch, "E266", {"points": [v(288.26, 343.75) * mm, v(282.52, 336.1) * mm, v(275.37, 332.25) * mm, v(266.85, 332.25) * mm]});
            skFitSpline(sketch, "E267", {"points": [v(266.85, 332.25) * mm, v(261.33, 332.25) * mm, v(256.9, 333.76) * mm, v(253.56, 336.78) * mm]});
            skFitSpline(sketch, "E268", {"points": [v(253.56, 336.78) * mm, v(250.21, 339.8) * mm, v(248.55, 343.84) * mm, v(248.55, 348.92) * mm]});
            skFitSpline(sketch, "E269", {"points": [v(248.55, 348.92) * mm, v(248.55, 358.85) * mm, v(254.08, 365.7) * mm, v(265.16, 369.52) * mm]});
            skFitSpline(sketch, "E270", {"points": [v(265.16, 369.52) * mm, v(261.45, 371.14) * mm, v(259.6, 374.46) * mm, v(259.6, 379.46) * mm]});
            skFitSpline(sketch, "E271", {"points": [v(259.6, 379.46) * mm, v(259.6, 383.85) * mm, v(261.34, 387.47) * mm, v(264.82, 390.34) * mm]});
            skFitSpline(sketch, "E272", {"points": [v(264.82, 390.34) * mm, v(268.3, 393.21) * mm, v(272.62, 394.65) * mm, v(277.79, 394.65) * mm]});
            skLineSegment(sketch, "E273", {"start": v(287.7, 359.33) * mm, "end": v(286.49, 359.8) * mm});
            skLineSegment(sketch, "E274", {"start": v(286.49, 359.8) * mm, "end": v(287.7, 359.33) * mm});
            skFitSpline(sketch, "E275", {"points": [v(277.79, 394.65) * mm, v(280.95, 394.65) * mm, v(283.67, 394.04) * mm, v(285.93, 392.83) * mm]});
            skFitSpline(sketch, "E276", {"points": [v(285.93, 392.83) * mm, v(288.2, 391.61) * mm, v(289.33, 390.05) * mm, v(289.33, 388.1) * mm]});
            skFitSpline(sketch, "E277", {"points": [v(289.33, 388.1) * mm, v(289.33, 386.55) * mm, v(288.3, 384.9) * mm, v(286.28, 383.13) * mm]});
            skFitSpline(sketch, "E278", {"points": [v(286.28, 383.13) * mm, v(284.16, 387.16) * mm, v(281.01, 389.18) * mm, v(276.84, 389.18) * mm]});
            skFitSpline(sketch, "E279", {"points": [v(276.84, 389.18) * mm, v(274.08, 389.18) * mm, v(271.82, 388.38) * mm, v(270.07, 386.75) * mm]});
            skFitSpline(sketch, "E280", {"points": [v(270.07, 386.75) * mm, v(268.32, 385.12) * mm, v(267.44, 383.06) * mm, v(267.44, 380.56) * mm]});
            skFitSpline(sketch, "E281", {"points": [v(267.44, 380.56) * mm, v(267.44, 377.66) * mm, v(268.8, 375.02) * mm, v(271.5, 372.69) * mm]});
            skFitSpline(sketch, "E282", {"points": [v(271.5, 372.69) * mm, v(273.4, 373.18) * mm, v(275.11, 373.43) * mm, v(276.63, 373.43) * mm]});
            skFitSpline(sketch, "E283", {"points": [v(276.63, 373.43) * mm, v(278.07, 373.43) * mm, v(279.73, 373.08) * mm, v(281.63, 372.4) * mm]});
            skFitSpline(sketch, "E284", {"points": [v(281.63, 372.4) * mm, v(280.16, 367.34) * mm, v(277.58, 364.81) * mm, v(273.88, 364.81) * mm]});
            skFitSpline(sketch, "E285", {"points": [v(273.88, 364.81) * mm, v(272.36, 364.81) * mm, v(270.86, 365.22) * mm, v(269.35, 366.02) * mm]});
            skFitSpline(sketch, "E286", {"points": [v(269.35, 366.02) * mm, v(265.7, 364.5) * mm, v(262.72, 362.19) * mm, v(260.42, 359.13) * mm]});
            skFitSpline(sketch, "E287", {"points": [v(260.42, 359.13) * mm, v(258.12, 356.06) * mm, v(256.96, 352.8) * mm, v(256.96, 349.32) * mm]});
            skFitSpline(sketch, "E288", {"points": [v(256.96, 349.32) * mm, v(256.96, 346.25) * mm, v(258.1, 343.74) * mm, v(260.39, 341.8) * mm]});
            skFitSpline(sketch, "E289", {"points": [v(260.39, 341.8) * mm, v(262.67, 339.86) * mm, v(265.66, 338.88) * mm, v(269.4, 338.88) * mm]});
            skFitSpline(sketch, "E290", {"points": [v(269.4, 338.88) * mm, v(273.9, 338.88) * mm, v(278.46, 340.78) * mm, v(283.03, 344.56) * mm]});
            skFitSpline(sketch, "E291", {"points": [v(283.03, 344.56) * mm, v(287.61, 348.33) * mm, v(289.9, 352.03) * mm, v(289.9, 355.63) * mm]});
            skFitSpline(sketch, "E292", {"points": [v(289.9, 355.63) * mm, v(289.9, 357.33) * mm, v(289.16, 358.57) * mm, v(287.7, 359.33) * mm]});
            skFitSpline(sketch, "E293", {"points": [v(286.49, 359.8) * mm, v(285.1, 360.5) * mm, v(284.39, 361.54) * mm, v(284.39, 362.92) * mm]});
            skFitSpline(sketch, "E294", {"points": [v(284.39, 362.92) * mm, v(284.39, 364.24) * mm, v(284.98, 366.15) * mm, v(286.17, 368.6) * mm]});
            skFitSpline(sketch, "E295", {"points": [v(286.17, 368.6) * mm, v(289.42, 367.14) * mm, v(293.87, 366.41) * mm, v(299.52, 366.41) * mm]});
            skFitSpline(sketch, "E296", {"points": [v(299.52, 366.41) * mm, v(302.52, 366.41) * mm, v(305.82, 366.82) * mm, v(309.44, 367.62) * mm]});
            skFitSpline(sketch, "E297", {"points": [v(309.44, 367.62) * mm, v(308.5, 363.93) * mm, v(307.32, 361.5) * mm, v(305.9, 360.33) * mm]});
            skFitSpline(sketch, "E298", {"points": [v(305.9, 360.33) * mm, v(304.46, 359.17) * mm, v(302.3, 358.6) * mm, v(299.4, 358.6) * mm]});
            skFitSpline(sketch, "E299", {"points": [v(299.4, 358.6) * mm, v(298.84, 358.6) * mm, v(298.17, 358.64) * mm, v(297.4, 358.75) * mm]});
            skFitSpline(sketch, "E300", {"points": [v(297.4, 358.75) * mm, v(294.74, 350.17) * mm, v(293.41, 343.18) * mm, v(293.41, 337.77) * mm]});
            skFitSpline(sketch, "E301", {"points": [v(293.41, 337.77) * mm, v(293.41, 333.72) * mm, v(294.08, 330.44) * mm, v(295.4, 327.95) * mm]});
            skFitSpline(sketch, "E302", {"points": [v(295.4, 327.95) * mm, v(293.52, 325.82) * mm, v(291.53, 324.77) * mm, v(289.43, 324.77) * mm]});
            skFitSpline(sketch, "E303", {"points": [v(289.43, 324.77) * mm, v(287.44, 324.77) * mm, v(286.45, 326.37) * mm, v(286.45, 329.58) * mm]});
            skFitSpline(sketch, "E304", {"points": [v(286.45, 329.58) * mm, v(286.45, 332.7) * mm, v(287.06, 337.43) * mm, v(288.26, 343.75) * mm]});
            skFitSpline(sketch, "E305", {"points": [v(288.26, 343.75) * mm, v(282.52, 336.1) * mm, v(275.37, 332.25) * mm, v(266.85, 332.25) * mm]});
            skFitSpline(sketch, "E306", {"points": [v(266.85, 332.25) * mm, v(261.33, 332.25) * mm, v(256.9, 333.76) * mm, v(253.56, 336.78) * mm]});
            skFitSpline(sketch, "E307", {"points": [v(253.56, 336.78) * mm, v(250.21, 339.8) * mm, v(248.55, 343.84) * mm, v(248.55, 348.92) * mm]});
            skFitSpline(sketch, "E308", {"points": [v(248.55, 348.92) * mm, v(248.55, 358.85) * mm, v(254.08, 365.7) * mm, v(265.16, 369.52) * mm]});
            skFitSpline(sketch, "E309", {"points": [v(265.16, 369.52) * mm, v(261.45, 371.14) * mm, v(259.6, 374.46) * mm, v(259.6, 379.46) * mm]});
            skFitSpline(sketch, "E310", {"points": [v(259.6, 379.46) * mm, v(259.6, 383.85) * mm, v(261.34, 387.47) * mm, v(264.82, 390.34) * mm]});
            skFitSpline(sketch, "E311", {"points": [v(264.82, 390.34) * mm, v(268.3, 393.21) * mm, v(272.62, 394.65) * mm, v(277.79, 394.65) * mm]});
            skFitSpline(sketch, "E312", {"points": [v(322.46, 256.65) * mm, v(318.75, 256.65) * mm, v(315.44, 254.74) * mm, v(312.52, 250.93) * mm]});
            skFitSpline(sketch, "E313", {"points": [v(312.52, 250.93) * mm, v(309.6, 247.1) * mm, v(308.14, 242.74) * mm, v(308.14, 237.81) * mm]});
            skFitSpline(sketch, "E314", {"points": [v(308.14, 237.81) * mm, v(308.14, 234.3) * mm, v(309, 231.42) * mm, v(310.71, 229.2) * mm]});
            skFitSpline(sketch, "E315", {"points": [v(310.71, 229.2) * mm, v(312.42, 227) * mm, v(314.6, 225.9) * mm, v(317.27, 225.9) * mm]});
            skFitSpline(sketch, "E316", {"points": [v(317.27, 225.9) * mm, v(320.96, 225.9) * mm, v(324.15, 228.04) * mm, v(326.87, 232.3) * mm]});
            skFitSpline(sketch, "E317", {"points": [v(326.87, 232.3) * mm, v(329.59, 236.57) * mm, v(330.95, 241.7) * mm, v(330.95, 247.66) * mm]});
            skFitSpline(sketch, "E318", {"points": [v(330.95, 247.66) * mm, v(330.95, 249.7) * mm, v(330.7, 251.56) * mm, v(330.2, 253.23) * mm]});
            skFitSpline(sketch, "E319", {"points": [v(330.2, 253.23) * mm, v(328.41, 253.83) * mm, v(326.72, 254.85) * mm, v(325.1, 256.27) * mm]});
            skFitSpline(sketch, "E320", {"points": [v(325.1, 256.27) * mm, v(324.07, 256.52) * mm, v(323.19, 256.65) * mm, v(322.46, 256.65) * mm]});
            skFitSpline(sketch, "E321", {"points": [v(240.42, 260.48) * mm, v(237.51, 260.48) * mm, v(234.78, 258.67) * mm, v(232.23, 255.02) * mm]});
            skFitSpline(sketch, "E322", {"points": [v(232.23, 255.02) * mm, v(229.66, 251.38) * mm, v(228.07, 247.23) * mm, v(227.45, 242.57) * mm]});
            skFitSpline(sketch, "E323", {"points": [v(227.45, 242.57) * mm, v(231.63, 242.83) * mm, v(235.4, 244.32) * mm, v(238.7, 247.04) * mm]});
            skFitSpline(sketch, "E324", {"points": [v(238.7, 247.04) * mm, v(242.03, 249.75) * mm, v(243.69, 252.82) * mm, v(243.69, 256.28) * mm]});
            skFitSpline(sketch, "E325", {"points": [v(243.69, 256.28) * mm, v(243.69, 259.09) * mm, v(242.6, 260.48) * mm, v(240.42, 260.48) * mm]});
            skFitSpline(sketch, "E326", {"points": [v(241.3, 265.95) * mm, v(244.47, 265.95) * mm, v(247.04, 265.03) * mm, v(249, 263.18) * mm]});
            skFitSpline(sketch, "E327", {"points": [v(249, 263.18) * mm, v(250.95, 261.35) * mm, v(251.93, 258.88) * mm, v(251.93, 255.8) * mm]});
            skFitSpline(sketch, "E328", {"points": [v(251.93, 255.8) * mm, v(251.93, 250.86) * mm, v(249.33, 246.53) * mm, v(244.16, 242.8) * mm]});
            skFitSpline(sketch, "E329", {"points": [v(244.16, 242.8) * mm, v(238.99, 239.07) * mm, v(233.32, 237.2) * mm, v(227.17, 237.2) * mm]});
            skFitSpline(sketch, "E330", {"points": [v(227.17, 237.2) * mm, v(227.17, 230.65) * mm, v(229.8, 227.37) * mm, v(235.06, 227.37) * mm]});
            skFitSpline(sketch, "E331", {"points": [v(235.06, 227.37) * mm, v(239.89, 227.37) * mm, v(245.25, 230) * mm, v(251.17, 235.25) * mm]});
            skFitSpline(sketch, "E332", {"points": [v(251.17, 235.25) * mm, v(256.88, 240.3) * mm, v(262.17, 247.06) * mm, v(267.04, 255.52) * mm]});
            skFitSpline(sketch, "E333", {"points": [v(267.04, 255.52) * mm, v(267.04, 255.63) * mm, v(267.05, 255.74) * mm, v(267.05, 255.84) * mm]});
            skFitSpline(sketch, "E334", {"points": [v(267.05, 255.84) * mm, v(267.05, 257.15) * mm, v(266.66, 258.53) * mm, v(265.9, 260) * mm]});
            skFitSpline(sketch, "E335", {"points": [v(265.9, 260) * mm, v(268.75, 261.23) * mm, v(270.96, 261.84) * mm, v(272.57, 261.84) * mm]});
            skFitSpline(sketch, "E336", {"points": [v(272.57, 261.84) * mm, v(274.69, 261.84) * mm, v(275.75, 260.41) * mm, v(275.75, 257.56) * mm]});
            skFitSpline(sketch, "E337", {"points": [v(275.75, 257.56) * mm, v(275.75, 256.1) * mm, v(275.15, 252.22) * mm, v(273.96, 245.95) * mm]});
            skFitSpline(sketch, "E338", {"points": [v(272.03, 235.67) * mm, v(275.54, 245) * mm, v(279.56, 252.4) * mm, v(284.1, 257.82) * mm]});
            skFitSpline(sketch, "E339", {"points": [v(284.1, 257.82) * mm, v(288.64, 263.24) * mm, v(292.83, 265.95) * mm, v(296.65, 265.95) * mm]});
            skFitSpline(sketch, "E340", {"points": [v(296.65, 265.95) * mm, v(298.1, 265.95) * mm, v(299.37, 265.46) * mm, v(300.46, 264.5) * mm]});
            skFitSpline(sketch, "E341", {"points": [v(300.46, 264.5) * mm, v(301.56, 263.54) * mm, v(302.1, 262.34) * mm, v(302.1, 260.93) * mm]});
            skFitSpline(sketch, "E342", {"points": [v(302.1, 260.93) * mm, v(302.1, 258.85) * mm, v(300, 256.15) * mm, v(295.8, 252.85) * mm]});
            skFitSpline(sketch, "E343", {"points": [v(295.8, 252.85) * mm, v(294.79, 254.9) * mm, v(293.62, 255.93) * mm, v(292.3, 255.93) * mm]});
            skFitSpline(sketch, "E344", {"points": [v(292.3, 255.93) * mm, v(289.6, 255.93) * mm, v(286.03, 252.53) * mm, v(281.6, 245.7) * mm]});
            skFitSpline(sketch, "E345", {"points": [v(281.6, 245.7) * mm, v(278.8, 241.39) * mm, v(276.38, 236.93) * mm, v(274.32, 232.34) * mm]});
            skFitSpline(sketch, "E346", {"points": [v(274.32, 232.34) * mm, v(272.26, 227.76) * mm, v(271.23, 224.47) * mm, v(271.23, 222.48) * mm]});
            skLineSegment(sketch, "E347", {"start": v(273.96, 245.95) * mm, "end": v(272.03, 235.67) * mm});
            skLineSegment(sketch, "E348", {"start": v(272.03, 235.67) * mm, "end": v(273.96, 245.95) * mm});
            skFitSpline(sketch, "E349", {"points": [v(271.27, 221.52) * mm, v(269.31, 220.47) * mm, v(267.8, 219.95) * mm, v(266.72, 219.95) * mm]});
            skFitSpline(sketch, "E350", {"points": [v(266.72, 219.95) * mm, v(263.89, 219.95) * mm, v(262.46, 221.4) * mm, v(262.46, 224.27) * mm]});
            skFitSpline(sketch, "E351", {"points": [v(262.46, 224.27) * mm, v(262.46, 225.52) * mm, v(262.89, 228.56) * mm, v(263.72, 233.37) * mm]});
            skLineSegment(sketch, "E352", {"start": v(271.23, 222.48) * mm, "end": v(271.27, 221.52) * mm});
            skLineSegment(sketch, "E353", {"start": v(271.27, 221.52) * mm, "end": v(271.23, 222.48) * mm});
            skFitSpline(sketch, "E354", {"points": [v(265.47, 243.21) * mm, v(261.99, 237.94) * mm, v(257.98, 233.36) * mm, v(253.47, 229.48) * mm]});
            skFitSpline(sketch, "E355", {"points": [v(253.47, 229.48) * mm, v(246.07, 223.13) * mm, v(239.03, 219.95) * mm, v(232.34, 219.95) * mm]});
            skFitSpline(sketch, "E356", {"points": [v(232.34, 219.95) * mm, v(227.94, 219.95) * mm, v(224.47, 221.55) * mm, v(221.91, 224.73) * mm]});
            skFitSpline(sketch, "E357", {"points": [v(221.91, 224.73) * mm, v(219.35, 227.92) * mm, v(218.07, 232.24) * mm, v(218.07, 237.69) * mm]});
            skFitSpline(sketch, "E358", {"points": [v(218.07, 237.69) * mm, v(218.07, 245.46) * mm, v(220.34, 252.12) * mm, v(224.87, 257.65) * mm]});
            skFitSpline(sketch, "E359", {"points": [v(224.87, 257.65) * mm, v(229.4, 263.18) * mm, v(234.88, 265.95) * mm, v(241.3, 265.95) * mm]});
            skLineSegment(sketch, "E360", {"start": v(263.72, 233.37) * mm, "end": v(265.46, 243.12) * mm});
            skLineSegment(sketch, "E361", {"start": v(265.46, 243.12) * mm, "end": v(265.47, 243.21) * mm});
            skLineSegment(sketch, "E362", {"start": v(265.47, 243.21) * mm, "end": v(263.72, 233.37) * mm});
            skFitSpline(sketch, "E363", {"points": [v(321.7, 268.35) * mm, v(327.88, 267.8) * mm, v(332.88, 264.45) * mm, v(336.73, 258.33) * mm]});
            skFitSpline(sketch, "E364", {"points": [v(336.73, 258.33) * mm, v(340.37, 255.54) * mm, v(344.2, 254.14) * mm, v(348.24, 254.14) * mm]});
            skFitSpline(sketch, "E365", {"points": [v(348.24, 254.14) * mm, v(349.7, 254.14) * mm, v(351.28, 254.46) * mm, v(353, 255.14) * mm]});
            skFitSpline(sketch, "E366", {"points": [v(353, 255.14) * mm, v(352.25, 256.33) * mm, v(351.5, 257.44) * mm, v(350.72, 258.45) * mm]});
            skFitSpline(sketch, "E367", {"points": [v(350.72, 258.45) * mm, v(352.74, 260.55) * mm, v(354.74, 261.6) * mm, v(356.73, 261.6) * mm]});
            skFitSpline(sketch, "E368", {"points": [v(356.73, 261.6) * mm, v(358.54, 261.6) * mm, v(360, 260.73) * mm, v(361.14, 259) * mm]});
            skFitSpline(sketch, "E369", {"points": [v(361.14, 259) * mm, v(362.27, 257.26) * mm, v(363.63, 254) * mm, v(365.2, 249.2) * mm]});
            skFitSpline(sketch, "E370", {"points": [v(365.2, 249.2) * mm, v(367.64, 241.7) * mm, v(369.34, 235.1) * mm, v(370.3, 229.37) * mm]});
            skFitSpline(sketch, "E371", {"points": [v(370.3, 229.37) * mm, v(377.47, 242.97) * mm, v(381.38, 255.16) * mm, v(382.06, 265.95) * mm]});
            skFitSpline(sketch, "E372", {"points": [v(382.06, 265.95) * mm, v(387.06, 265.2) * mm, v(389.57, 263.4) * mm, v(389.57, 260.57) * mm]});
            skFitSpline(sketch, "E373", {"points": [v(389.57, 260.57) * mm, v(389.57, 257.95) * mm, v(387.72, 252.7) * mm, v(384.02, 244.83) * mm]});
            skFitSpline(sketch, "E374", {"points": [v(384.02, 244.83) * mm, v(380.32, 236.96) * mm, v(376.35, 229.75) * mm, v(372.1, 223.22) * mm]});
            skFitSpline(sketch, "E375", {"points": [v(372.1, 223.22) * mm, v(367.2, 215.7) * mm, v(362.28, 209.74) * mm, v(357.38, 205.33) * mm]});
            skFitSpline(sketch, "E376", {"points": [v(357.38, 205.33) * mm, v(352.47, 200.93) * mm, v(348.2, 198.73) * mm, v(344.57, 198.73) * mm]});
            skFitSpline(sketch, "E377", {"points": [v(344.57, 198.73) * mm, v(340.98, 198.73) * mm, v(339.18, 200.47) * mm, v(339.18, 203.94) * mm]});
            skFitSpline(sketch, "E378", {"points": [v(339.18, 203.94) * mm, v(339.18, 205.24) * mm, v(339.59, 206.91) * mm, v(340.38, 208.95) * mm]});
            skFitSpline(sketch, "E379", {"points": [v(340.38, 208.95) * mm, v(342.03, 208.07) * mm, v(343.73, 207.63) * mm, v(345.47, 207.63) * mm]});
            skFitSpline(sketch, "E380", {"points": [v(345.47, 207.63) * mm, v(352.03, 207.63) * mm, v(358.3, 212.46) * mm, v(364.27, 222.14) * mm]});
            skFitSpline(sketch, "E381", {"points": [v(364.27, 222.14) * mm, v(363.28, 228.86) * mm, v(361.54, 235.6) * mm, v(359.02, 242.38) * mm]});
            skFitSpline(sketch, "E382", {"points": [v(359.02, 242.38) * mm, v(357.95, 245.25) * mm, v(356.83, 247.88) * mm, v(355.67, 250.25) * mm]});
            skFitSpline(sketch, "E383", {"points": [v(355.67, 250.25) * mm, v(352.93, 248.72) * mm, v(350.19, 247.96) * mm, v(347.44, 247.96) * mm]});
            skFitSpline(sketch, "E384", {"points": [v(347.44, 247.96) * mm, v(344.78, 247.96) * mm, v(342.1, 248.56) * mm, v(339.4, 249.76) * mm]});
            skFitSpline(sketch, "E385", {"points": [v(339.4, 249.76) * mm, v(339.48, 249.66) * mm, v(339.5, 249.36) * mm, v(339.5, 248.87) * mm]});
            skFitSpline(sketch, "E386", {"points": [v(339.5, 248.87) * mm, v(339.5, 241.14) * mm, v(337.16, 234.38) * mm, v(332.49, 228.6) * mm]});
            skFitSpline(sketch, "E387", {"points": [v(332.49, 228.6) * mm, v(327.8, 222.83) * mm, v(322.3, 219.95) * mm, v(315.95, 219.95) * mm]});
            skFitSpline(sketch, "E388", {"points": [v(315.95, 219.95) * mm, v(311.1, 219.95) * mm, v(307.12, 221.7) * mm, v(304.05, 225.22) * mm]});
            skFitSpline(sketch, "E389", {"points": [v(304.05, 225.22) * mm, v(300.98, 228.72) * mm, v(299.44, 233.26) * mm, v(299.44, 238.82) * mm]});
            skFitSpline(sketch, "E390", {"points": [v(299.44, 238.82) * mm, v(299.44, 245.12) * mm, v(301.4, 250.58) * mm, v(305.33, 255.2) * mm]});
            skFitSpline(sketch, "E391", {"points": [v(305.33, 255.2) * mm, v(309.26, 259.81) * mm, v(313.9, 262.12) * mm, v(319.26, 262.12) * mm]});
            skFitSpline(sketch, "E392", {"points": [v(319.26, 262.12) * mm, v(320.1, 262.12) * mm, v(320.7, 262) * mm, v(321.06, 261.76) * mm]});
            skFitSpline(sketch, "E393", {"points": [v(321.06, 261.76) * mm, v(320.47, 262.26) * mm, v(320.19, 263) * mm, v(320.19, 263.94) * mm]});
            skFitSpline(sketch, "E394", {"points": [v(320.19, 263.94) * mm, v(320.19, 265.37) * mm, v(320.7, 266.85) * mm, v(321.7, 268.35) * mm]});
            skFitSpline(sketch, "E395", {"points": [v(190.94, 286.25) * mm, v(192.87, 286.25) * mm, v(193.84, 285.06) * mm, v(193.84, 282.68) * mm]});
            skFitSpline(sketch, "E396", {"points": [v(193.84, 282.68) * mm, v(193.84, 282.18) * mm, v(193.44, 279.75) * mm, v(192.63, 275.4) * mm]});
            skFitSpline(sketch, "E397", {"points": [v(186.62, 241.34) * mm, v(185.75, 236.5) * mm, v(185.32, 233.12) * mm, v(185.32, 231.22) * mm]});
            skFitSpline(sketch, "E398", {"points": [v(185.32, 231.22) * mm, v(185.32, 228.5) * mm, v(188.28, 227.13) * mm, v(194.21, 227.13) * mm]});
            skFitSpline(sketch, "E399", {"points": [v(194.21, 227.13) * mm, v(199.86, 227.13) * mm, v(206.02, 228.45) * mm, v(212.68, 231.08) * mm]});
            skFitSpline(sketch, "E400", {"points": [v(212.68, 231.08) * mm, v(211.84, 227.71) * mm, v(210.86, 225.39) * mm, v(209.73, 224.13) * mm]});
            skFitSpline(sketch, "E401", {"points": [v(209.73, 224.13) * mm, v(208.6, 222.84) * mm, v(205.85, 221.75) * mm, v(201.5, 220.86) * mm]});
            skFitSpline(sketch, "E402", {"points": [v(201.5, 220.86) * mm, v(197.16, 219.96) * mm, v(192.62, 219.5) * mm, v(187.87, 219.5) * mm]});
            skFitSpline(sketch, "E403", {"points": [v(187.87, 219.5) * mm, v(179.99, 219.5) * mm, v(176.05, 222.62) * mm, v(176.05, 228.83) * mm]});
            skFitSpline(sketch, "E404", {"points": [v(176.05, 228.83) * mm, v(176.05, 230.48) * mm, v(176.44, 233.54) * mm, v(177.24, 238.01) * mm]});
            skLineSegment(sketch, "E405", {"start": v(192.63, 275.4) * mm, "end": v(186.62, 241.34) * mm});
            skLineSegment(sketch, "E406", {"start": v(186.62, 241.34) * mm, "end": v(192.63, 275.4) * mm});
            skFitSpline(sketch, "E407", {"points": [v(184.03, 276.41) * mm, v(184.41, 278.6) * mm, v(184.6, 280.13) * mm, v(184.6, 281.03) * mm]});
            skFitSpline(sketch, "E408", {"points": [v(184.6, 281.03) * mm, v(184.6, 281.73) * mm, v(184.33, 282.67) * mm, v(183.79, 283.85) * mm]});
            skFitSpline(sketch, "E409", {"points": [v(183.79, 283.85) * mm, v(187.28, 285.45) * mm, v(189.66, 286.25) * mm, v(190.94, 286.25) * mm]});
            skLineSegment(sketch, "E410", {"start": v(177.24, 238.01) * mm, "end": v(184.03, 276.41) * mm});
            skLineSegment(sketch, "E411", {"start": v(184.03, 276.41) * mm, "end": v(177.24, 238.01) * mm});
            skFitSpline(sketch, "E412", {"points": [v(322.46, 256.65) * mm, v(318.75, 256.65) * mm, v(315.44, 254.74) * mm, v(312.52, 250.93) * mm]});
            skFitSpline(sketch, "E413", {"points": [v(312.52, 250.93) * mm, v(309.6, 247.1) * mm, v(308.14, 242.74) * mm, v(308.14, 237.81) * mm]});
            skFitSpline(sketch, "E414", {"points": [v(308.14, 237.81) * mm, v(308.14, 234.3) * mm, v(309, 231.42) * mm, v(310.71, 229.2) * mm]});
            skFitSpline(sketch, "E415", {"points": [v(310.71, 229.2) * mm, v(312.42, 227) * mm, v(314.6, 225.9) * mm, v(317.27, 225.9) * mm]});
            skFitSpline(sketch, "E416", {"points": [v(317.27, 225.9) * mm, v(320.96, 225.9) * mm, v(324.15, 228.04) * mm, v(326.87, 232.3) * mm]});
            skFitSpline(sketch, "E417", {"points": [v(326.87, 232.3) * mm, v(329.59, 236.57) * mm, v(330.95, 241.7) * mm, v(330.95, 247.66) * mm]});
            skFitSpline(sketch, "E418", {"points": [v(330.95, 247.66) * mm, v(330.95, 249.7) * mm, v(330.7, 251.56) * mm, v(330.2, 253.23) * mm]});
            skFitSpline(sketch, "E419", {"points": [v(330.2, 253.23) * mm, v(328.41, 253.83) * mm, v(326.72, 254.85) * mm, v(325.1, 256.27) * mm]});
            skFitSpline(sketch, "E420", {"points": [v(325.1, 256.27) * mm, v(324.07, 256.52) * mm, v(323.19, 256.65) * mm, v(322.46, 256.65) * mm]});
            skFitSpline(sketch, "E421", {"points": [v(240.42, 260.48) * mm, v(237.51, 260.48) * mm, v(234.78, 258.67) * mm, v(232.23, 255.02) * mm]});
            skFitSpline(sketch, "E422", {"points": [v(232.23, 255.02) * mm, v(229.66, 251.38) * mm, v(228.07, 247.23) * mm, v(227.45, 242.57) * mm]});
            skFitSpline(sketch, "E423", {"points": [v(227.45, 242.57) * mm, v(231.63, 242.83) * mm, v(235.4, 244.32) * mm, v(238.7, 247.04) * mm]});
            skFitSpline(sketch, "E424", {"points": [v(238.7, 247.04) * mm, v(242.03, 249.75) * mm, v(243.69, 252.82) * mm, v(243.69, 256.28) * mm]});
            skFitSpline(sketch, "E425", {"points": [v(243.69, 256.28) * mm, v(243.69, 259.09) * mm, v(242.6, 260.48) * mm, v(240.42, 260.48) * mm]});
            skFitSpline(sketch, "E426", {"points": [v(241.3, 265.95) * mm, v(244.47, 265.95) * mm, v(247.04, 265.03) * mm, v(249, 263.18) * mm]});
            skFitSpline(sketch, "E427", {"points": [v(249, 263.18) * mm, v(250.95, 261.35) * mm, v(251.93, 258.88) * mm, v(251.93, 255.8) * mm]});
            skFitSpline(sketch, "E428", {"points": [v(251.93, 255.8) * mm, v(251.93, 250.86) * mm, v(249.33, 246.53) * mm, v(244.16, 242.8) * mm]});
            skFitSpline(sketch, "E429", {"points": [v(244.16, 242.8) * mm, v(238.99, 239.07) * mm, v(233.32, 237.2) * mm, v(227.17, 237.2) * mm]});
            skFitSpline(sketch, "E430", {"points": [v(227.17, 237.2) * mm, v(227.17, 230.65) * mm, v(229.8, 227.37) * mm, v(235.06, 227.37) * mm]});
            skFitSpline(sketch, "E431", {"points": [v(235.06, 227.37) * mm, v(239.89, 227.37) * mm, v(245.25, 230) * mm, v(251.17, 235.25) * mm]});
            skFitSpline(sketch, "E432", {"points": [v(251.17, 235.25) * mm, v(256.88, 240.3) * mm, v(262.17, 247.06) * mm, v(267.04, 255.52) * mm]});
            skFitSpline(sketch, "E433", {"points": [v(267.04, 255.52) * mm, v(267.04, 255.63) * mm, v(267.05, 255.74) * mm, v(267.05, 255.84) * mm]});
            skFitSpline(sketch, "E434", {"points": [v(267.05, 255.84) * mm, v(267.05, 257.15) * mm, v(266.66, 258.53) * mm, v(265.9, 260) * mm]});
            skFitSpline(sketch, "E435", {"points": [v(265.9, 260) * mm, v(268.75, 261.23) * mm, v(270.96, 261.84) * mm, v(272.57, 261.84) * mm]});
            skFitSpline(sketch, "E436", {"points": [v(272.57, 261.84) * mm, v(274.69, 261.84) * mm, v(275.75, 260.41) * mm, v(275.75, 257.56) * mm]});
            skFitSpline(sketch, "E437", {"points": [v(275.75, 257.56) * mm, v(275.75, 256.1) * mm, v(275.15, 252.22) * mm, v(273.96, 245.95) * mm]});
            skFitSpline(sketch, "E438", {"points": [v(272.03, 235.67) * mm, v(275.54, 245) * mm, v(279.56, 252.4) * mm, v(284.1, 257.82) * mm]});
            skFitSpline(sketch, "E439", {"points": [v(284.1, 257.82) * mm, v(288.64, 263.24) * mm, v(292.83, 265.95) * mm, v(296.65, 265.95) * mm]});
            skFitSpline(sketch, "E440", {"points": [v(296.65, 265.95) * mm, v(298.1, 265.95) * mm, v(299.37, 265.46) * mm, v(300.46, 264.5) * mm]});
            skFitSpline(sketch, "E441", {"points": [v(300.46, 264.5) * mm, v(301.56, 263.54) * mm, v(302.1, 262.34) * mm, v(302.1, 260.93) * mm]});
            skFitSpline(sketch, "E442", {"points": [v(302.1, 260.93) * mm, v(302.1, 258.85) * mm, v(300, 256.15) * mm, v(295.8, 252.85) * mm]});
            skFitSpline(sketch, "E443", {"points": [v(295.8, 252.85) * mm, v(294.79, 254.9) * mm, v(293.62, 255.93) * mm, v(292.3, 255.93) * mm]});
            skFitSpline(sketch, "E444", {"points": [v(292.3, 255.93) * mm, v(289.6, 255.93) * mm, v(286.03, 252.53) * mm, v(281.6, 245.7) * mm]});
            skFitSpline(sketch, "E445", {"points": [v(281.6, 245.7) * mm, v(278.8, 241.39) * mm, v(276.38, 236.93) * mm, v(274.32, 232.34) * mm]});
            skFitSpline(sketch, "E446", {"points": [v(274.32, 232.34) * mm, v(272.26, 227.76) * mm, v(271.23, 224.47) * mm, v(271.23, 222.48) * mm]});
            skFitSpline(sketch, "E447", {"points": [v(271.27, 221.52) * mm, v(269.31, 220.47) * mm, v(267.8, 219.95) * mm, v(266.72, 219.95) * mm]});
            skFitSpline(sketch, "E448", {"points": [v(266.72, 219.95) * mm, v(263.89, 219.95) * mm, v(262.46, 221.4) * mm, v(262.46, 224.27) * mm]});
            skFitSpline(sketch, "E449", {"points": [v(262.46, 224.27) * mm, v(262.46, 225.52) * mm, v(262.89, 228.56) * mm, v(263.72, 233.37) * mm]});
            skFitSpline(sketch, "E450", {"points": [v(265.47, 243.21) * mm, v(261.99, 237.94) * mm, v(257.98, 233.36) * mm, v(253.47, 229.48) * mm]});
            skFitSpline(sketch, "E451", {"points": [v(253.47, 229.48) * mm, v(246.07, 223.13) * mm, v(239.03, 219.95) * mm, v(232.34, 219.95) * mm]});
            skFitSpline(sketch, "E452", {"points": [v(232.34, 219.95) * mm, v(227.94, 219.95) * mm, v(224.47, 221.55) * mm, v(221.91, 224.73) * mm]});
            skFitSpline(sketch, "E453", {"points": [v(221.91, 224.73) * mm, v(219.35, 227.92) * mm, v(218.07, 232.24) * mm, v(218.07, 237.69) * mm]});
            skFitSpline(sketch, "E454", {"points": [v(218.07, 237.69) * mm, v(218.07, 245.46) * mm, v(220.34, 252.12) * mm, v(224.87, 257.65) * mm]});
            skFitSpline(sketch, "E455", {"points": [v(224.87, 257.65) * mm, v(229.4, 263.18) * mm, v(234.88, 265.95) * mm, v(241.3, 265.95) * mm]});
            skFitSpline(sketch, "E456", {"points": [v(321.7, 268.35) * mm, v(327.88, 267.8) * mm, v(332.88, 264.45) * mm, v(336.73, 258.33) * mm]});
            skFitSpline(sketch, "E457", {"points": [v(336.73, 258.33) * mm, v(340.37, 255.54) * mm, v(344.2, 254.14) * mm, v(348.24, 254.14) * mm]});
            skFitSpline(sketch, "E458", {"points": [v(348.24, 254.14) * mm, v(349.7, 254.14) * mm, v(351.28, 254.46) * mm, v(353, 255.14) * mm]});
            skFitSpline(sketch, "E459", {"points": [v(353, 255.14) * mm, v(352.25, 256.33) * mm, v(351.5, 257.44) * mm, v(350.72, 258.45) * mm]});
            skFitSpline(sketch, "E460", {"points": [v(350.72, 258.45) * mm, v(352.74, 260.55) * mm, v(354.74, 261.6) * mm, v(356.73, 261.6) * mm]});
            skFitSpline(sketch, "E461", {"points": [v(356.73, 261.6) * mm, v(358.54, 261.6) * mm, v(360, 260.73) * mm, v(361.14, 259) * mm]});
            skFitSpline(sketch, "E462", {"points": [v(361.14, 259) * mm, v(362.27, 257.26) * mm, v(363.63, 254) * mm, v(365.2, 249.2) * mm]});
            skFitSpline(sketch, "E463", {"points": [v(365.2, 249.2) * mm, v(367.64, 241.7) * mm, v(369.34, 235.1) * mm, v(370.3, 229.37) * mm]});
            skFitSpline(sketch, "E464", {"points": [v(370.3, 229.37) * mm, v(377.47, 242.97) * mm, v(381.38, 255.16) * mm, v(382.06, 265.95) * mm]});
            skFitSpline(sketch, "E465", {"points": [v(382.06, 265.95) * mm, v(387.06, 265.2) * mm, v(389.57, 263.4) * mm, v(389.57, 260.57) * mm]});
            skFitSpline(sketch, "E466", {"points": [v(389.57, 260.57) * mm, v(389.57, 257.95) * mm, v(387.72, 252.7) * mm, v(384.02, 244.83) * mm]});
            skFitSpline(sketch, "E467", {"points": [v(384.02, 244.83) * mm, v(380.32, 236.96) * mm, v(376.35, 229.75) * mm, v(372.1, 223.22) * mm]});
            skFitSpline(sketch, "E468", {"points": [v(372.1, 223.22) * mm, v(367.2, 215.7) * mm, v(362.28, 209.74) * mm, v(357.38, 205.33) * mm]});
            skFitSpline(sketch, "E469", {"points": [v(357.38, 205.33) * mm, v(352.47, 200.93) * mm, v(348.2, 198.73) * mm, v(344.57, 198.73) * mm]});
            skFitSpline(sketch, "E470", {"points": [v(344.57, 198.73) * mm, v(340.98, 198.73) * mm, v(339.18, 200.47) * mm, v(339.18, 203.94) * mm]});
            skFitSpline(sketch, "E471", {"points": [v(339.18, 203.94) * mm, v(339.18, 205.24) * mm, v(339.59, 206.91) * mm, v(340.38, 208.95) * mm]});
            skFitSpline(sketch, "E472", {"points": [v(340.38, 208.95) * mm, v(342.03, 208.07) * mm, v(343.73, 207.63) * mm, v(345.47, 207.63) * mm]});
            skFitSpline(sketch, "E473", {"points": [v(345.47, 207.63) * mm, v(352.03, 207.63) * mm, v(358.3, 212.46) * mm, v(364.27, 222.14) * mm]});
            skFitSpline(sketch, "E474", {"points": [v(364.27, 222.14) * mm, v(363.28, 228.86) * mm, v(361.54, 235.6) * mm, v(359.02, 242.38) * mm]});
            skFitSpline(sketch, "E475", {"points": [v(359.02, 242.38) * mm, v(357.95, 245.25) * mm, v(356.83, 247.88) * mm, v(355.67, 250.25) * mm]});
            skFitSpline(sketch, "E476", {"points": [v(355.67, 250.25) * mm, v(352.93, 248.72) * mm, v(350.19, 247.96) * mm, v(347.44, 247.96) * mm]});
            skFitSpline(sketch, "E477", {"points": [v(347.44, 247.96) * mm, v(344.78, 247.96) * mm, v(342.1, 248.56) * mm, v(339.4, 249.76) * mm]});
            skFitSpline(sketch, "E478", {"points": [v(339.4, 249.76) * mm, v(339.48, 249.66) * mm, v(339.5, 249.36) * mm, v(339.5, 248.87) * mm]});
            skFitSpline(sketch, "E479", {"points": [v(339.5, 248.87) * mm, v(339.5, 241.14) * mm, v(337.16, 234.38) * mm, v(332.49, 228.6) * mm]});
            skFitSpline(sketch, "E480", {"points": [v(332.49, 228.6) * mm, v(327.8, 222.83) * mm, v(322.3, 219.95) * mm, v(315.95, 219.95) * mm]});
            skFitSpline(sketch, "E481", {"points": [v(315.95, 219.95) * mm, v(311.1, 219.95) * mm, v(307.12, 221.7) * mm, v(304.05, 225.22) * mm]});
            skFitSpline(sketch, "E482", {"points": [v(304.05, 225.22) * mm, v(300.98, 228.72) * mm, v(299.44, 233.26) * mm, v(299.44, 238.82) * mm]});
            skFitSpline(sketch, "E483", {"points": [v(299.44, 238.82) * mm, v(299.44, 245.12) * mm, v(301.4, 250.58) * mm, v(305.33, 255.2) * mm]});
            skFitSpline(sketch, "E484", {"points": [v(305.33, 255.2) * mm, v(309.26, 259.81) * mm, v(313.9, 262.12) * mm, v(319.26, 262.12) * mm]});
            skFitSpline(sketch, "E485", {"points": [v(319.26, 262.12) * mm, v(320.1, 262.12) * mm, v(320.7, 262) * mm, v(321.06, 261.76) * mm]});
            skFitSpline(sketch, "E486", {"points": [v(321.06, 261.76) * mm, v(320.47, 262.26) * mm, v(320.19, 263) * mm, v(320.19, 263.94) * mm]});
            skFitSpline(sketch, "E487", {"points": [v(320.19, 263.94) * mm, v(320.19, 265.37) * mm, v(320.7, 266.85) * mm, v(321.7, 268.35) * mm]});
            skFitSpline(sketch, "E488", {"points": [v(190.94, 286.25) * mm, v(192.87, 286.25) * mm, v(193.84, 285.06) * mm, v(193.84, 282.68) * mm]});
            skFitSpline(sketch, "E489", {"points": [v(193.84, 282.68) * mm, v(193.84, 282.18) * mm, v(193.44, 279.75) * mm, v(192.63, 275.4) * mm]});
            skFitSpline(sketch, "E490", {"points": [v(186.62, 241.34) * mm, v(185.75, 236.5) * mm, v(185.32, 233.12) * mm, v(185.32, 231.22) * mm]});
            skFitSpline(sketch, "E491", {"points": [v(185.32, 231.22) * mm, v(185.32, 228.5) * mm, v(188.28, 227.13) * mm, v(194.21, 227.13) * mm]});
            skFitSpline(sketch, "E492", {"points": [v(194.21, 227.13) * mm, v(199.86, 227.13) * mm, v(206.02, 228.45) * mm, v(212.68, 231.08) * mm]});
            skFitSpline(sketch, "E493", {"points": [v(212.68, 231.08) * mm, v(211.84, 227.71) * mm, v(210.86, 225.39) * mm, v(209.73, 224.13) * mm]});
            skFitSpline(sketch, "E494", {"points": [v(209.73, 224.13) * mm, v(208.6, 222.84) * mm, v(205.85, 221.75) * mm, v(201.5, 220.86) * mm]});
            skFitSpline(sketch, "E495", {"points": [v(201.5, 220.86) * mm, v(197.16, 219.96) * mm, v(192.62, 219.5) * mm, v(187.87, 219.5) * mm]});
            skFitSpline(sketch, "E496", {"points": [v(187.87, 219.5) * mm, v(179.99, 219.5) * mm, v(176.05, 222.62) * mm, v(176.05, 228.83) * mm]});
            skFitSpline(sketch, "E497", {"points": [v(176.05, 228.83) * mm, v(176.05, 230.48) * mm, v(176.44, 233.54) * mm, v(177.24, 238.01) * mm]});
            skFitSpline(sketch, "E498", {"points": [v(184.03, 276.41) * mm, v(184.41, 278.6) * mm, v(184.6, 280.13) * mm, v(184.6, 281.03) * mm]});
            skFitSpline(sketch, "E499", {"points": [v(184.6, 281.03) * mm, v(184.6, 281.73) * mm, v(184.33, 282.67) * mm, v(183.79, 283.85) * mm]});
            skFitSpline(sketch, "E500", {"points": [v(183.79, 283.85) * mm, v(187.28, 285.45) * mm, v(189.66, 286.25) * mm, v(190.94, 286.25) * mm]});
            skFitSpline(sketch, "E501", {"points": [v(148.9, 160.76) * mm, v(152.84, 160.76) * mm, v(156.03, 159.69) * mm, v(158.5, 157.52) * mm]});
            skFitSpline(sketch, "E502", {"points": [v(158.5, 157.52) * mm, v(160.96, 155.36) * mm, v(162.2, 152.5) * mm, v(162.2, 148.95) * mm]});
            skFitSpline(sketch, "E503", {"points": [v(162.2, 148.95) * mm, v(162.2, 139.05) * mm, v(152.73, 125.67) * mm, v(133.82, 108.83) * mm]});
            skFitSpline(sketch, "E504", {"points": [v(133.82, 108.83) * mm, v(141.2, 110.02) * mm, v(147.51, 110.62) * mm, v(152.72, 110.62) * mm]});
            skFitSpline(sketch, "E505", {"points": [v(152.72, 110.62) * mm, v(156.78, 110.62) * mm, v(159.46, 109.94) * mm, v(160.79, 108.57) * mm]});
            skFitSpline(sketch, "E506", {"points": [v(160.79, 108.57) * mm, v(162.11, 107.2) * mm, v(162.93, 103.95) * mm, v(163.25, 98.82) * mm]});
            skFitSpline(sketch, "E507", {"points": [v(163.25, 98.82) * mm, v(159.1, 100.65) * mm, v(154.02, 101.57) * mm, v(148.06, 101.57) * mm]});
            skFitSpline(sketch, "E508", {"points": [v(148.06, 101.57) * mm, v(143.16, 101.57) * mm, v(138.24, 101.13) * mm, v(133.32, 100.27) * mm]});
            skFitSpline(sketch, "E509", {"points": [v(131.2, 99.92) * mm, v(129.2, 99.58) * mm, v(127.89, 99.4) * mm, v(127.26, 99.4) * mm]});
            skFitSpline(sketch, "E510", {"points": [v(127.26, 99.4) * mm, v(125.1, 99.4) * mm, v(124.04, 100.8) * mm, v(124.04, 103.6) * mm]});
            skFitSpline(sketch, "E511", {"points": [v(124.04, 103.6) * mm, v(124.04, 104.4) * mm, v(124.14, 105.62) * mm, v(124.32, 107.24) * mm]});
            skFitSpline(sketch, "E512", {"points": [v(124.32, 107.24) * mm, v(132.32, 113.12) * mm, v(139.12, 119.9) * mm, v(144.71, 127.63) * mm]});
            skFitSpline(sketch, "E513", {"points": [v(144.71, 127.63) * mm, v(150.3, 135.35) * mm, v(153.1, 141.66) * mm, v(153.1, 146.57) * mm]});
            skFitSpline(sketch, "E514", {"points": [v(153.1, 146.57) * mm, v(153.1, 151.09) * mm, v(150.85, 153.34) * mm, v(146.35, 153.34) * mm]});
            skFitSpline(sketch, "E515", {"points": [v(146.35, 153.34) * mm, v(140.98, 153.34) * mm, v(135.91, 149.75) * mm, v(131.13, 142.53) * mm]});
            skFitSpline(sketch, "E516", {"points": [v(131.13, 142.53) * mm, v(130.6, 144.51) * mm, v(130.34, 146) * mm, v(130.34, 147.01) * mm]});
            skFitSpline(sketch, "E517", {"points": [v(130.34, 147.01) * mm, v(130.34, 150.43) * mm, v(132.32, 153.57) * mm, v(136.28, 156.45) * mm]});
            skFitSpline(sketch, "E518", {"points": [v(136.28, 156.45) * mm, v(140.24, 159.33) * mm, v(144.45, 160.76) * mm, v(148.9, 160.76) * mm]});
            skLineSegment(sketch, "E519", {"start": v(133.32, 100.27) * mm, "end": v(131.2, 99.92) * mm});
            skLineSegment(sketch, "E520", {"start": v(131.2, 99.92) * mm, "end": v(133.32, 100.27) * mm});
            skFitSpline(sketch, "E521", {"points": [v(148.9, 160.76) * mm, v(152.84, 160.76) * mm, v(156.03, 159.69) * mm, v(158.5, 157.52) * mm]});
            skFitSpline(sketch, "E522", {"points": [v(158.5, 157.52) * mm, v(160.96, 155.36) * mm, v(162.2, 152.5) * mm, v(162.2, 148.95) * mm]});
            skFitSpline(sketch, "E523", {"points": [v(162.2, 148.95) * mm, v(162.2, 139.05) * mm, v(152.73, 125.67) * mm, v(133.82, 108.83) * mm]});
            skFitSpline(sketch, "E524", {"points": [v(133.82, 108.83) * mm, v(141.2, 110.02) * mm, v(147.51, 110.62) * mm, v(152.72, 110.62) * mm]});
            skFitSpline(sketch, "E525", {"points": [v(152.72, 110.62) * mm, v(156.78, 110.62) * mm, v(159.46, 109.94) * mm, v(160.79, 108.57) * mm]});
            skFitSpline(sketch, "E526", {"points": [v(160.79, 108.57) * mm, v(162.11, 107.2) * mm, v(162.93, 103.95) * mm, v(163.25, 98.82) * mm]});
            skFitSpline(sketch, "E527", {"points": [v(163.25, 98.82) * mm, v(159.1, 100.65) * mm, v(154.02, 101.57) * mm, v(148.06, 101.57) * mm]});
            skFitSpline(sketch, "E528", {"points": [v(148.06, 101.57) * mm, v(143.16, 101.57) * mm, v(138.24, 101.13) * mm, v(133.32, 100.27) * mm]});
            skFitSpline(sketch, "E529", {"points": [v(131.2, 99.92) * mm, v(129.2, 99.58) * mm, v(127.89, 99.4) * mm, v(127.26, 99.4) * mm]});
            skFitSpline(sketch, "E530", {"points": [v(127.26, 99.4) * mm, v(125.1, 99.4) * mm, v(124.04, 100.8) * mm, v(124.04, 103.6) * mm]});
            skFitSpline(sketch, "E531", {"points": [v(124.04, 103.6) * mm, v(124.04, 104.4) * mm, v(124.14, 105.62) * mm, v(124.32, 107.24) * mm]});
            skFitSpline(sketch, "E532", {"points": [v(124.32, 107.24) * mm, v(132.32, 113.12) * mm, v(139.12, 119.9) * mm, v(144.71, 127.63) * mm]});
            skFitSpline(sketch, "E533", {"points": [v(144.71, 127.63) * mm, v(150.3, 135.35) * mm, v(153.1, 141.66) * mm, v(153.1, 146.57) * mm]});
            skFitSpline(sketch, "E534", {"points": [v(153.1, 146.57) * mm, v(153.1, 151.09) * mm, v(150.85, 153.34) * mm, v(146.35, 153.34) * mm]});
            skFitSpline(sketch, "E535", {"points": [v(146.35, 153.34) * mm, v(140.98, 153.34) * mm, v(135.91, 149.75) * mm, v(131.13, 142.53) * mm]});
            skFitSpline(sketch, "E536", {"points": [v(131.13, 142.53) * mm, v(130.6, 144.51) * mm, v(130.34, 146) * mm, v(130.34, 147.01) * mm]});
            skFitSpline(sketch, "E537", {"points": [v(130.34, 147.01) * mm, v(130.34, 150.43) * mm, v(132.32, 153.57) * mm, v(136.28, 156.45) * mm]});
            skFitSpline(sketch, "E538", {"points": [v(136.28, 156.45) * mm, v(140.24, 159.33) * mm, v(144.45, 160.76) * mm, v(148.9, 160.76) * mm]});
            skFitSpline(sketch, "E539", {"points": [v(202.2, 129.7) * mm, v(201.44, 123.52) * mm, v(199.56, 120.44) * mm, v(196.58, 120.44) * mm]});
            skFitSpline(sketch, "E540", {"points": [v(196.58, 120.44) * mm, v(195.93, 120.44) * mm, v(195.18, 120.5) * mm, v(194.33, 120.6) * mm]});
            skFitSpline(sketch, "E541", {"points": [v(191.57, 120.98) * mm, v(189.87, 121.23) * mm, v(188.55, 121.35) * mm, v(187.62, 121.35) * mm]});
            skFitSpline(sketch, "E542", {"points": [v(187.62, 121.35) * mm, v(186.31, 121.35) * mm, v(184.66, 120.96) * mm, v(182.65, 120.15) * mm]});
            skFitSpline(sketch, "E543", {"points": [v(182.65, 120.15) * mm, v(184.1, 125.83) * mm, v(186.47, 128.65) * mm, v(189.74, 128.65) * mm]});
            skFitSpline(sketch, "E544", {"points": [v(189.74, 128.65) * mm, v(190.3, 128.65) * mm, v(190.9, 128.6) * mm, v(191.57, 128.53) * mm]});
            skLineSegment(sketch, "E545", {"start": v(194.33, 120.6) * mm, "end": v(191.57, 120.98) * mm});
            skLineSegment(sketch, "E546", {"start": v(191.57, 120.98) * mm, "end": v(194.33, 120.6) * mm});
            skFitSpline(sketch, "E547", {"points": [v(195.42, 128.04) * mm, v(196.04, 127.97) * mm, v(196.72, 127.94) * mm, v(197.45, 127.94) * mm]});
            skFitSpline(sketch, "E548", {"points": [v(197.45, 127.94) * mm, v(199.07, 127.94) * mm, v(200.66, 128.53) * mm, v(202.2, 129.7) * mm]});
            skLineSegment(sketch, "E549", {"start": v(191.57, 128.53) * mm, "end": v(195.42, 128.04) * mm});
            skLineSegment(sketch, "E550", {"start": v(195.42, 128.04) * mm, "end": v(191.57, 128.53) * mm});
            skFitSpline(sketch, "E551", {"points": [v(202.2, 129.7) * mm, v(201.44, 123.52) * mm, v(199.56, 120.44) * mm, v(196.58, 120.44) * mm]});
            skFitSpline(sketch, "E552", {"points": [v(196.58, 120.44) * mm, v(195.93, 120.44) * mm, v(195.18, 120.5) * mm, v(194.33, 120.6) * mm]});
            skFitSpline(sketch, "E553", {"points": [v(191.57, 120.98) * mm, v(189.87, 121.23) * mm, v(188.55, 121.35) * mm, v(187.62, 121.35) * mm]});
            skFitSpline(sketch, "E554", {"points": [v(187.62, 121.35) * mm, v(186.31, 121.35) * mm, v(184.66, 120.96) * mm, v(182.65, 120.15) * mm]});
            skFitSpline(sketch, "E555", {"points": [v(182.65, 120.15) * mm, v(184.1, 125.83) * mm, v(186.47, 128.65) * mm, v(189.74, 128.65) * mm]});
            skFitSpline(sketch, "E556", {"points": [v(189.74, 128.65) * mm, v(190.3, 128.65) * mm, v(190.9, 128.6) * mm, v(191.57, 128.53) * mm]});
            skFitSpline(sketch, "E557", {"points": [v(195.42, 128.04) * mm, v(196.04, 127.97) * mm, v(196.72, 127.94) * mm, v(197.45, 127.94) * mm]});
            skFitSpline(sketch, "E558", {"points": [v(197.45, 127.94) * mm, v(199.07, 127.94) * mm, v(200.66, 128.53) * mm, v(202.2, 129.7) * mm]});
            skFitSpline(sketch, "E559", {"points": [v(231.1, 107.4) * mm, v(233.12, 107.8) * mm, v(234.8, 107.99) * mm, v(236.16, 107.99) * mm]});
            skFitSpline(sketch, "E560", {"points": [v(236.16, 107.99) * mm, v(239.42, 107.99) * mm, v(241.64, 107.39) * mm, v(242.8, 106.17) * mm]});
            skFitSpline(sketch, "E561", {"points": [v(242.8, 106.17) * mm, v(243.98, 104.96) * mm, v(244.56, 102.4) * mm, v(244.56, 98.48) * mm]});
            skFitSpline(sketch, "E562", {"points": [v(244.56, 98.48) * mm, v(242.68, 99.4) * mm, v(240.77, 99.85) * mm, v(238.84, 99.85) * mm]});
            skFitSpline(sketch, "E563", {"points": [v(238.84, 99.85) * mm, v(236.6, 99.85) * mm, v(233.83, 99.62) * mm, v(230.56, 99.18) * mm]});
            skLineSegment(sketch, "E564", {"start": v(240.33, 160.84) * mm, "end": v(231.1, 107.4) * mm});
            skLineSegment(sketch, "E565", {"start": v(231.1, 107.4) * mm, "end": v(240.33, 160.84) * mm});
            skFitSpline(sketch, "E566", {"points": [v(225.68, 98.5) * mm, v(224.08, 98.26) * mm, v(221.9, 97.9) * mm, v(219.13, 97.41) * mm]});
            skFitSpline(sketch, "E567", {"points": [v(219.13, 97.41) * mm, v(218.25, 97.25) * mm, v(217.34, 97.17) * mm, v(216.4, 97.17) * mm]});
            skFitSpline(sketch, "E568", {"points": [v(216.4, 97.17) * mm, v(213.42, 97.17) * mm, v(211.7, 100.17) * mm, v(211.24, 106.14) * mm]});
            skFitSpline(sketch, "E569", {"points": [v(211.24, 106.14) * mm, v(213.04, 105.46) * mm, v(214.48, 105.12) * mm, v(215.58, 105.12) * mm]});
            skFitSpline(sketch, "E570", {"points": [v(215.58, 105.12) * mm, v(218.04, 105.12) * mm, v(220.36, 105.41) * mm, v(222.57, 106) * mm]});
            skLineSegment(sketch, "E571", {"start": v(230.56, 99.18) * mm, "end": v(225.68, 98.5) * mm});
            skLineSegment(sketch, "E572", {"start": v(225.68, 98.5) * mm, "end": v(230.56, 99.18) * mm});
            skFitSpline(sketch, "E573", {"points": [v(230.14, 148.1) * mm, v(226.91, 146) * mm, v(224.12, 144.93) * mm, v(221.77, 144.93) * mm]});
            skFitSpline(sketch, "E574", {"points": [v(221.77, 144.93) * mm, v(217.95, 144.93) * mm, v(216.04, 147.62) * mm, v(216.04, 153.01) * mm]});
            skLineSegment(sketch, "E575", {"start": v(222.57, 106) * mm, "end": v(230.14, 148.1) * mm});
            skLineSegment(sketch, "E576", {"start": v(230.14, 148.1) * mm, "end": v(222.57, 106) * mm});
            skFitSpline(sketch, "E577", {"points": [v(216.04, 154.9) * mm, v(218.1, 153.52) * mm, v(219.94, 152.83) * mm, v(221.59, 152.83) * mm]});
            skFitSpline(sketch, "E578", {"points": [v(221.59, 152.83) * mm, v(224.5, 152.83) * mm, v(229.56, 155.03) * mm, v(236.73, 159.44) * mm]});
            skFitSpline(sketch, "E579", {"points": [v(236.73, 159.44) * mm, v(237.05, 159.62) * mm, v(238.25, 160.1) * mm, v(240.33, 160.84) * mm]});
            skLineSegment(sketch, "E580", {"start": v(216.04, 153.01) * mm, "end": v(216.04, 154.9) * mm});
            skLineSegment(sketch, "E581", {"start": v(216.04, 154.9) * mm, "end": v(216.04, 153.01) * mm});
            skFitSpline(sketch, "E582", {"points": [v(231.1, 107.4) * mm, v(233.12, 107.8) * mm, v(234.8, 107.99) * mm, v(236.16, 107.99) * mm]});
            skFitSpline(sketch, "E583", {"points": [v(236.16, 107.99) * mm, v(239.42, 107.99) * mm, v(241.64, 107.39) * mm, v(242.8, 106.17) * mm]});
            skFitSpline(sketch, "E584", {"points": [v(242.8, 106.17) * mm, v(243.98, 104.96) * mm, v(244.56, 102.4) * mm, v(244.56, 98.48) * mm]});
            skFitSpline(sketch, "E585", {"points": [v(244.56, 98.48) * mm, v(242.68, 99.4) * mm, v(240.77, 99.85) * mm, v(238.84, 99.85) * mm]});
            skFitSpline(sketch, "E586", {"points": [v(238.84, 99.85) * mm, v(236.6, 99.85) * mm, v(233.83, 99.62) * mm, v(230.56, 99.18) * mm]});
            skFitSpline(sketch, "E587", {"points": [v(225.68, 98.5) * mm, v(224.08, 98.26) * mm, v(221.9, 97.9) * mm, v(219.13, 97.41) * mm]});
            skFitSpline(sketch, "E588", {"points": [v(219.13, 97.41) * mm, v(218.25, 97.25) * mm, v(217.34, 97.17) * mm, v(216.4, 97.17) * mm]});
            skFitSpline(sketch, "E589", {"points": [v(216.4, 97.17) * mm, v(213.42, 97.17) * mm, v(211.7, 100.17) * mm, v(211.24, 106.14) * mm]});
            skFitSpline(sketch, "E590", {"points": [v(211.24, 106.14) * mm, v(213.04, 105.46) * mm, v(214.48, 105.12) * mm, v(215.58, 105.12) * mm]});
            skFitSpline(sketch, "E591", {"points": [v(215.58, 105.12) * mm, v(218.04, 105.12) * mm, v(220.36, 105.41) * mm, v(222.57, 106) * mm]});
            skFitSpline(sketch, "E592", {"points": [v(230.14, 148.1) * mm, v(226.91, 146) * mm, v(224.12, 144.93) * mm, v(221.77, 144.93) * mm]});
            skFitSpline(sketch, "E593", {"points": [v(221.77, 144.93) * mm, v(217.95, 144.93) * mm, v(216.04, 147.62) * mm, v(216.04, 153.01) * mm]});
            skFitSpline(sketch, "E594", {"points": [v(216.04, 154.9) * mm, v(218.1, 153.52) * mm, v(219.94, 152.83) * mm, v(221.59, 152.83) * mm]});
            skFitSpline(sketch, "E595", {"points": [v(221.59, 152.83) * mm, v(224.5, 152.83) * mm, v(229.56, 155.03) * mm, v(236.73, 159.44) * mm]});
            skFitSpline(sketch, "E596", {"points": [v(236.73, 159.44) * mm, v(237.05, 159.62) * mm, v(238.25, 160.1) * mm, v(240.33, 160.84) * mm]});
            skFitSpline(sketch, "E597", {"points": [v(280.08, 107.4) * mm, v(282.1, 107.8) * mm, v(283.8, 107.99) * mm, v(285.15, 107.99) * mm]});
            skFitSpline(sketch, "E598", {"points": [v(285.15, 107.99) * mm, v(288.4, 107.99) * mm, v(290.62, 107.39) * mm, v(291.8, 106.17) * mm]});
            skFitSpline(sketch, "E599", {"points": [v(291.8, 106.17) * mm, v(292.97, 104.96) * mm, v(293.54, 102.4) * mm, v(293.54, 98.48) * mm]});
            skFitSpline(sketch, "E600", {"points": [v(293.54, 98.48) * mm, v(291.66, 99.4) * mm, v(289.75, 99.85) * mm, v(287.82, 99.85) * mm]});
            skFitSpline(sketch, "E601", {"points": [v(287.82, 99.85) * mm, v(285.58, 99.85) * mm, v(282.82, 99.62) * mm, v(279.55, 99.18) * mm]});
            skLineSegment(sketch, "E602", {"start": v(289.32, 160.84) * mm, "end": v(280.08, 107.4) * mm});
            skLineSegment(sketch, "E603", {"start": v(280.08, 107.4) * mm, "end": v(289.32, 160.84) * mm});
            skFitSpline(sketch, "E604", {"points": [v(274.67, 98.5) * mm, v(273.07, 98.26) * mm, v(270.89, 97.9) * mm, v(268.12, 97.41) * mm]});
            skFitSpline(sketch, "E605", {"points": [v(268.12, 97.41) * mm, v(267.24, 97.25) * mm, v(266.33, 97.17) * mm, v(265.4, 97.17) * mm]});
            skFitSpline(sketch, "E606", {"points": [v(265.4, 97.17) * mm, v(262.41, 97.17) * mm, v(260.68, 100.17) * mm, v(260.23, 106.14) * mm]});
            skFitSpline(sketch, "E607", {"points": [v(260.23, 106.14) * mm, v(262.03, 105.46) * mm, v(263.47, 105.12) * mm, v(264.56, 105.12) * mm]});
            skFitSpline(sketch, "E608", {"points": [v(264.56, 105.12) * mm, v(267.03, 105.12) * mm, v(269.35, 105.41) * mm, v(271.55, 106) * mm]});
            skLineSegment(sketch, "E609", {"start": v(279.55, 99.18) * mm, "end": v(274.67, 98.5) * mm});
            skLineSegment(sketch, "E610", {"start": v(274.67, 98.5) * mm, "end": v(279.55, 99.18) * mm});
            skFitSpline(sketch, "E611", {"points": [v(279.12, 148.1) * mm, v(275.9, 146) * mm, v(273.11, 144.93) * mm, v(270.76, 144.93) * mm]});
            skFitSpline(sketch, "E612", {"points": [v(270.76, 144.93) * mm, v(266.94, 144.93) * mm, v(265.03, 147.62) * mm, v(265.03, 153.01) * mm]});
            skLineSegment(sketch, "E613", {"start": v(271.55, 106) * mm, "end": v(279.12, 148.1) * mm});
            skLineSegment(sketch, "E614", {"start": v(279.12, 148.1) * mm, "end": v(271.55, 106) * mm});
            skFitSpline(sketch, "E615", {"points": [v(265.03, 154.9) * mm, v(267.08, 153.52) * mm, v(268.93, 152.83) * mm, v(270.57, 152.83) * mm]});
            skFitSpline(sketch, "E616", {"points": [v(270.57, 152.83) * mm, v(273.5, 152.83) * mm, v(278.55, 155.03) * mm, v(285.72, 159.44) * mm]});
            skFitSpline(sketch, "E617", {"points": [v(285.72, 159.44) * mm, v(286.03, 159.62) * mm, v(287.24, 160.1) * mm, v(289.32, 160.84) * mm]});
            skLineSegment(sketch, "E618", {"start": v(265.03, 153.01) * mm, "end": v(265.03, 154.9) * mm});
            skLineSegment(sketch, "E619", {"start": v(265.03, 154.9) * mm, "end": v(265.03, 153.01) * mm});
            skFitSpline(sketch, "E620", {"points": [v(280.08, 107.4) * mm, v(282.1, 107.8) * mm, v(283.8, 107.99) * mm, v(285.15, 107.99) * mm]});
            skFitSpline(sketch, "E621", {"points": [v(285.15, 107.99) * mm, v(288.4, 107.99) * mm, v(290.62, 107.39) * mm, v(291.8, 106.17) * mm]});
            skFitSpline(sketch, "E622", {"points": [v(291.8, 106.17) * mm, v(292.97, 104.96) * mm, v(293.54, 102.4) * mm, v(293.54, 98.48) * mm]});
            skFitSpline(sketch, "E623", {"points": [v(293.54, 98.48) * mm, v(291.66, 99.4) * mm, v(289.75, 99.85) * mm, v(287.82, 99.85) * mm]});
            skFitSpline(sketch, "E624", {"points": [v(287.82, 99.85) * mm, v(285.58, 99.85) * mm, v(282.82, 99.62) * mm, v(279.55, 99.18) * mm]});
            skFitSpline(sketch, "E625", {"points": [v(274.67, 98.5) * mm, v(273.07, 98.26) * mm, v(270.89, 97.9) * mm, v(268.12, 97.41) * mm]});
            skFitSpline(sketch, "E626", {"points": [v(268.12, 97.41) * mm, v(267.24, 97.25) * mm, v(266.33, 97.17) * mm, v(265.4, 97.17) * mm]});
            skFitSpline(sketch, "E627", {"points": [v(265.4, 97.17) * mm, v(262.41, 97.17) * mm, v(260.68, 100.17) * mm, v(260.23, 106.14) * mm]});
            skFitSpline(sketch, "E628", {"points": [v(260.23, 106.14) * mm, v(262.03, 105.46) * mm, v(263.47, 105.12) * mm, v(264.56, 105.12) * mm]});
            skFitSpline(sketch, "E629", {"points": [v(264.56, 105.12) * mm, v(267.03, 105.12) * mm, v(269.35, 105.41) * mm, v(271.55, 106) * mm]});
            skFitSpline(sketch, "E630", {"points": [v(279.12, 148.1) * mm, v(275.9, 146) * mm, v(273.11, 144.93) * mm, v(270.76, 144.93) * mm]});
            skFitSpline(sketch, "E631", {"points": [v(270.76, 144.93) * mm, v(266.94, 144.93) * mm, v(265.03, 147.62) * mm, v(265.03, 153.01) * mm]});
            skFitSpline(sketch, "E632", {"points": [v(265.03, 154.9) * mm, v(267.08, 153.52) * mm, v(268.93, 152.83) * mm, v(270.57, 152.83) * mm]});
            skFitSpline(sketch, "E633", {"points": [v(270.57, 152.83) * mm, v(273.5, 152.83) * mm, v(278.55, 155.03) * mm, v(285.72, 159.44) * mm]});
            skFitSpline(sketch, "E634", {"points": [v(285.72, 159.44) * mm, v(286.03, 159.62) * mm, v(287.24, 160.1) * mm, v(289.32, 160.84) * mm]});
            skFitSpline(sketch, "E635", {"points": [v(335.1, 129.7) * mm, v(334.33, 123.52) * mm, v(332.46, 120.44) * mm, v(329.47, 120.44) * mm]});
            skFitSpline(sketch, "E636", {"points": [v(329.47, 120.44) * mm, v(328.83, 120.44) * mm, v(328.08, 120.5) * mm, v(327.22, 120.6) * mm]});
            skFitSpline(sketch, "E637", {"points": [v(324.46, 120.98) * mm, v(322.76, 121.23) * mm, v(321.44, 121.35) * mm, v(320.51, 121.35) * mm]});
            skFitSpline(sketch, "E638", {"points": [v(320.51, 121.35) * mm, v(319.2, 121.35) * mm, v(317.55, 120.96) * mm, v(315.55, 120.15) * mm]});
            skFitSpline(sketch, "E639", {"points": [v(315.55, 120.15) * mm, v(317, 125.83) * mm, v(319.37, 128.65) * mm, v(322.63, 128.65) * mm]});
            skFitSpline(sketch, "E640", {"points": [v(322.63, 128.65) * mm, v(323.19, 128.65) * mm, v(323.8, 128.6) * mm, v(324.46, 128.53) * mm]});
            skLineSegment(sketch, "E641", {"start": v(327.22, 120.6) * mm, "end": v(324.46, 120.98) * mm});
            skLineSegment(sketch, "E642", {"start": v(324.46, 120.98) * mm, "end": v(327.22, 120.6) * mm});
            skFitSpline(sketch, "E643", {"points": [v(328.31, 128.04) * mm, v(328.94, 127.97) * mm, v(329.62, 127.94) * mm, v(330.34, 127.94) * mm]});
            skFitSpline(sketch, "E644", {"points": [v(330.34, 127.94) * mm, v(331.97, 127.94) * mm, v(333.56, 128.53) * mm, v(335.1, 129.7) * mm]});
            skLineSegment(sketch, "E645", {"start": v(324.46, 128.53) * mm, "end": v(328.31, 128.04) * mm});
            skLineSegment(sketch, "E646", {"start": v(328.31, 128.04) * mm, "end": v(324.46, 128.53) * mm});
            skFitSpline(sketch, "E647", {"points": [v(335.1, 129.7) * mm, v(334.33, 123.52) * mm, v(332.46, 120.44) * mm, v(329.47, 120.44) * mm]});
            skFitSpline(sketch, "E648", {"points": [v(329.47, 120.44) * mm, v(328.83, 120.44) * mm, v(328.08, 120.5) * mm, v(327.22, 120.6) * mm]});
            skFitSpline(sketch, "E649", {"points": [v(324.46, 120.98) * mm, v(322.76, 121.23) * mm, v(321.44, 121.35) * mm, v(320.51, 121.35) * mm]});
            skFitSpline(sketch, "E650", {"points": [v(320.51, 121.35) * mm, v(319.2, 121.35) * mm, v(317.55, 120.96) * mm, v(315.55, 120.15) * mm]});
            skFitSpline(sketch, "E651", {"points": [v(315.55, 120.15) * mm, v(317, 125.83) * mm, v(319.37, 128.65) * mm, v(322.63, 128.65) * mm]});
            skFitSpline(sketch, "E652", {"points": [v(322.63, 128.65) * mm, v(323.19, 128.65) * mm, v(323.8, 128.6) * mm, v(324.46, 128.53) * mm]});
            skFitSpline(sketch, "E653", {"points": [v(328.31, 128.04) * mm, v(328.94, 127.97) * mm, v(329.62, 127.94) * mm, v(330.34, 127.94) * mm]});
            skFitSpline(sketch, "E654", {"points": [v(330.34, 127.94) * mm, v(331.97, 127.94) * mm, v(333.56, 128.53) * mm, v(335.1, 129.7) * mm]});
            skFitSpline(sketch, "E655", {"points": [v(364.48, 107.4) * mm, v(366.5, 107.8) * mm, v(368.19, 107.99) * mm, v(369.54, 107.99) * mm]});
            skFitSpline(sketch, "E656", {"points": [v(369.54, 107.99) * mm, v(372.8, 107.99) * mm, v(375.02, 107.39) * mm, v(376.19, 106.17) * mm]});
            skFitSpline(sketch, "E657", {"points": [v(376.19, 106.17) * mm, v(377.36, 104.96) * mm, v(377.94, 102.4) * mm, v(377.94, 98.48) * mm]});
            skFitSpline(sketch, "E658", {"points": [v(377.94, 98.48) * mm, v(376.06, 99.4) * mm, v(374.15, 99.85) * mm, v(372.22, 99.85) * mm]});
            skFitSpline(sketch, "E659", {"points": [v(372.22, 99.85) * mm, v(369.97, 99.85) * mm, v(367.22, 99.62) * mm, v(363.94, 99.18) * mm]});
            skLineSegment(sketch, "E660", {"start": v(373.71, 160.84) * mm, "end": v(364.48, 107.4) * mm});
            skLineSegment(sketch, "E661", {"start": v(364.48, 107.4) * mm, "end": v(373.71, 160.84) * mm});
            skFitSpline(sketch, "E662", {"points": [v(359.06, 98.5) * mm, v(357.46, 98.26) * mm, v(355.28, 97.9) * mm, v(352.51, 97.41) * mm]});
            skFitSpline(sketch, "E663", {"points": [v(352.51, 97.41) * mm, v(351.63, 97.25) * mm, v(350.72, 97.17) * mm, v(349.78, 97.17) * mm]});
            skFitSpline(sketch, "E664", {"points": [v(349.78, 97.17) * mm, v(346.8, 97.17) * mm, v(345.08, 100.17) * mm, v(344.62, 106.14) * mm]});
            skFitSpline(sketch, "E665", {"points": [v(344.62, 106.14) * mm, v(346.42, 105.46) * mm, v(347.86, 105.12) * mm, v(348.96, 105.12) * mm]});
            skFitSpline(sketch, "E666", {"points": [v(348.96, 105.12) * mm, v(351.42, 105.12) * mm, v(353.75, 105.41) * mm, v(355.95, 106) * mm]});
            skLineSegment(sketch, "E667", {"start": v(363.94, 99.18) * mm, "end": v(359.06, 98.5) * mm});
            skLineSegment(sketch, "E668", {"start": v(359.06, 98.5) * mm, "end": v(363.94, 99.18) * mm});
            skFitSpline(sketch, "E669", {"points": [v(363.52, 148.1) * mm, v(360.3, 146) * mm, v(357.5, 144.93) * mm, v(355.15, 144.93) * mm]});
            skFitSpline(sketch, "E670", {"points": [v(355.15, 144.93) * mm, v(351.33, 144.93) * mm, v(349.42, 147.62) * mm, v(349.42, 153.01) * mm]});
            skLineSegment(sketch, "E671", {"start": v(355.95, 106) * mm, "end": v(363.52, 148.1) * mm});
            skLineSegment(sketch, "E672", {"start": v(363.52, 148.1) * mm, "end": v(355.95, 106) * mm});
            skFitSpline(sketch, "E673", {"points": [v(349.42, 154.9) * mm, v(351.47, 153.52) * mm, v(353.32, 152.83) * mm, v(354.97, 152.83) * mm]});
            skFitSpline(sketch, "E674", {"points": [v(354.97, 152.83) * mm, v(357.89, 152.83) * mm, v(362.94, 155.03) * mm, v(370.12, 159.44) * mm]});
            skFitSpline(sketch, "E675", {"points": [v(370.12, 159.44) * mm, v(370.43, 159.62) * mm, v(371.63, 160.1) * mm, v(373.71, 160.84) * mm]});
            skLineSegment(sketch, "E676", {"start": v(349.42, 153.01) * mm, "end": v(349.42, 154.9) * mm});
            skLineSegment(sketch, "E677", {"start": v(349.42, 154.9) * mm, "end": v(349.42, 153.01) * mm});
            skFitSpline(sketch, "E678", {"points": [v(399.53, 161.29) * mm, v(401.74, 160.06) * mm, v(404.75, 159.45) * mm, v(408.55, 159.45) * mm]});
            skFitSpline(sketch, "E679", {"points": [v(432.57, 150.65) * mm, v(425.06, 143.33) * mm, v(418.97, 135.14) * mm, v(414.28, 126.1) * mm]});
            skFitSpline(sketch, "E680", {"points": [v(414.28, 126.1) * mm, v(409.6, 117.05) * mm, v(407.25, 109.05) * mm, v(407.25, 102.1) * mm]});
            skFitSpline(sketch, "E681", {"points": [v(407.25, 102.1) * mm, v(407.25, 100.52) * mm, v(407.42, 98.58) * mm, v(407.77, 96.28) * mm]});
            skFitSpline(sketch, "E682", {"points": [v(407.77, 96.28) * mm, v(406.64, 95.93) * mm, v(405.75, 95.74) * mm, v(405.08, 95.74) * mm]});
            skFitSpline(sketch, "E683", {"points": [v(405.08, 95.74) * mm, v(400.09, 95.74) * mm, v(397.59, 97.79) * mm, v(397.59, 101.86) * mm]});
            skFitSpline(sketch, "E684", {"points": [v(397.59, 101.86) * mm, v(397.59, 104.73) * mm, v(398.72, 109.17) * mm, v(401, 115.15) * mm]});
            skFitSpline(sketch, "E685", {"points": [v(401, 115.15) * mm, v(403.29, 121.13) * mm, v(405.8, 126.31) * mm, v(408.57, 130.72) * mm]});
            skFitSpline(sketch, "E686", {"points": [v(408.57, 130.72) * mm, v(414.11, 139.56) * mm, v(419.76, 146.08) * mm, v(425.54, 150.28) * mm]});
            skLineSegment(sketch, "E687", {"start": v(408.55, 159.45) * mm, "end": v(410.1, 159.48) * mm});
            skLineSegment(sketch, "E688", {"start": v(410.1, 159.48) * mm, "end": v(414.9, 159.4) * mm});
            skLineSegment(sketch, "E689", {"start": v(414.9, 159.4) * mm, "end": v(419.69, 159.33) * mm});
            skLineSegment(sketch, "E690", {"start": v(419.69, 159.33) * mm, "end": v(433.97, 159.33) * mm});
            skLineSegment(sketch, "E691", {"start": v(433.97, 159.33) * mm, "end": v(432.57, 150.65) * mm});
            skFitSpline(sketch, "E692", {"points": [v(411.55, 150.23) * mm, v(406.34, 150.23) * mm, v(402.84, 150.48) * mm, v(401.06, 150.98) * mm]});
            skFitSpline(sketch, "E693", {"points": [v(401.06, 150.98) * mm, v(399.28, 151.48) * mm, v(398.39, 152.65) * mm, v(398.39, 154.51) * mm]});
            skFitSpline(sketch, "E694", {"points": [v(398.39, 154.51) * mm, v(398.39, 155.11) * mm, v(398.47, 155.9) * mm, v(398.64, 156.83) * mm]});
            skFitSpline(sketch, "E695", {"points": [v(398.64, 156.83) * mm, v(398.73, 157.24) * mm, v(398.84, 157.8) * mm, v(398.98, 158.52) * mm]});
            skLineSegment(sketch, "E696", {"start": v(413.55, 150.28) * mm, "end": v(411.55, 150.23) * mm});
            skLineSegment(sketch, "E697", {"start": v(411.55, 150.23) * mm, "end": v(424.28, 150.28) * mm});
            skLineSegment(sketch, "E698", {"start": v(398.98, 158.52) * mm, "end": v(399.53, 161.29) * mm});
            skLineSegment(sketch, "E699", {"start": v(399.53, 161.29) * mm, "end": v(398.98, 158.52) * mm});
            skFitSpline(sketch, "E700", {"points": [v(364.48, 107.4) * mm, v(366.5, 107.8) * mm, v(368.19, 107.99) * mm, v(369.54, 107.99) * mm]});
            skFitSpline(sketch, "E701", {"points": [v(369.54, 107.99) * mm, v(372.8, 107.99) * mm, v(375.02, 107.39) * mm, v(376.19, 106.17) * mm]});
            skFitSpline(sketch, "E702", {"points": [v(376.19, 106.17) * mm, v(377.36, 104.96) * mm, v(377.94, 102.4) * mm, v(377.94, 98.48) * mm]});
            skFitSpline(sketch, "E703", {"points": [v(377.94, 98.48) * mm, v(376.06, 99.4) * mm, v(374.15, 99.85) * mm, v(372.22, 99.85) * mm]});
            skFitSpline(sketch, "E704", {"points": [v(372.22, 99.85) * mm, v(369.97, 99.85) * mm, v(367.22, 99.62) * mm, v(363.94, 99.18) * mm]});
            skFitSpline(sketch, "E705", {"points": [v(359.06, 98.5) * mm, v(357.46, 98.26) * mm, v(355.28, 97.9) * mm, v(352.51, 97.41) * mm]});
            skFitSpline(sketch, "E706", {"points": [v(352.51, 97.41) * mm, v(351.63, 97.25) * mm, v(350.72, 97.17) * mm, v(349.78, 97.17) * mm]});
            skFitSpline(sketch, "E707", {"points": [v(349.78, 97.17) * mm, v(346.8, 97.17) * mm, v(345.08, 100.17) * mm, v(344.62, 106.14) * mm]});
            skFitSpline(sketch, "E708", {"points": [v(344.62, 106.14) * mm, v(346.42, 105.46) * mm, v(347.86, 105.12) * mm, v(348.96, 105.12) * mm]});
            skFitSpline(sketch, "E709", {"points": [v(348.96, 105.12) * mm, v(351.42, 105.12) * mm, v(353.75, 105.41) * mm, v(355.95, 106) * mm]});
            skFitSpline(sketch, "E710", {"points": [v(363.52, 148.1) * mm, v(360.3, 146) * mm, v(357.5, 144.93) * mm, v(355.15, 144.93) * mm]});
            skFitSpline(sketch, "E711", {"points": [v(355.15, 144.93) * mm, v(351.33, 144.93) * mm, v(349.42, 147.62) * mm, v(349.42, 153.01) * mm]});
            skFitSpline(sketch, "E712", {"points": [v(349.42, 154.9) * mm, v(351.47, 153.52) * mm, v(353.32, 152.83) * mm, v(354.97, 152.83) * mm]});
            skFitSpline(sketch, "E713", {"points": [v(354.97, 152.83) * mm, v(357.89, 152.83) * mm, v(362.94, 155.03) * mm, v(370.12, 159.44) * mm]});
            skFitSpline(sketch, "E714", {"points": [v(370.12, 159.44) * mm, v(370.43, 159.62) * mm, v(371.63, 160.1) * mm, v(373.71, 160.84) * mm]});
            skFitSpline(sketch, "E715", {"points": [v(399.53, 161.29) * mm, v(401.74, 160.06) * mm, v(404.75, 159.45) * mm, v(408.55, 159.45) * mm]});
            skFitSpline(sketch, "E716", {"points": [v(432.57, 150.65) * mm, v(425.06, 143.33) * mm, v(418.97, 135.14) * mm, v(414.28, 126.1) * mm]});
            skFitSpline(sketch, "E717", {"points": [v(414.28, 126.1) * mm, v(409.6, 117.05) * mm, v(407.25, 109.05) * mm, v(407.25, 102.1) * mm]});
            skFitSpline(sketch, "E718", {"points": [v(407.25, 102.1) * mm, v(407.25, 100.52) * mm, v(407.42, 98.58) * mm, v(407.77, 96.28) * mm]});
            skFitSpline(sketch, "E719", {"points": [v(407.77, 96.28) * mm, v(406.64, 95.93) * mm, v(405.75, 95.74) * mm, v(405.08, 95.74) * mm]});
            skFitSpline(sketch, "E720", {"points": [v(405.08, 95.74) * mm, v(400.09, 95.74) * mm, v(397.59, 97.79) * mm, v(397.59, 101.86) * mm]});
            skFitSpline(sketch, "E721", {"points": [v(397.59, 101.86) * mm, v(397.59, 104.73) * mm, v(398.72, 109.17) * mm, v(401, 115.15) * mm]});
            skFitSpline(sketch, "E722", {"points": [v(401, 115.15) * mm, v(403.29, 121.13) * mm, v(405.8, 126.31) * mm, v(408.57, 130.72) * mm]});
            skFitSpline(sketch, "E723", {"points": [v(408.57, 130.72) * mm, v(414.11, 139.56) * mm, v(419.76, 146.08) * mm, v(425.54, 150.28) * mm]});
            skFitSpline(sketch, "E724", {"points": [v(411.55, 150.23) * mm, v(406.34, 150.23) * mm, v(402.84, 150.48) * mm, v(401.06, 150.98) * mm]});
            skFitSpline(sketch, "E725", {"points": [v(401.06, 150.98) * mm, v(399.28, 151.48) * mm, v(398.39, 152.65) * mm, v(398.39, 154.51) * mm]});
            skFitSpline(sketch, "E726", {"points": [v(398.39, 154.51) * mm, v(398.39, 155.11) * mm, v(398.47, 155.9) * mm, v(398.64, 156.83) * mm]});
            skFitSpline(sketch, "E727", {"points": [v(398.64, 156.83) * mm, v(398.73, 157.24) * mm, v(398.84, 157.8) * mm, v(398.98, 158.52) * mm]});
            skLineSegment(sketch, "E728", {"start": v(279.4, 609.6) * mm, "end": v(278.58, 0) * mm, "construction": true});
            skArc(sketch, "E729.filletArc", {"start": v(134.87, 109.77) * mm, "mid": v(134.78, 109.28) * mm, "end": v(135.22, 109.05) * mm});
            skArc(sketch, "E730.filletArc", {"start": v(424.54, 149.53) * mm, "mid": v(424.68, 150) * mm, "end": v(424.28, 150.28) * mm});
            skSolve(sketch);
        }
        {
            var Q0;
            Q0=qSketchRegion(id+"F2",true);
            extrude(context, id + "F3", {"entities" : qUnion([Q0]), "operationType" : NewBodyOperationType.REMOVE, "oppositeDirection" : true, "depth" : 4.76 * mm});
        }
        {
            var Q0;
            {var subQ0=sQuery(id+"F0.wireOp",EDGE,"E4.filletArc");var subQ1=sQuery(id+"F0.wireOp",EDGE,"E3.filletArc");var subQ2=sQuery(id+"F0.wireOp",EDGE,"E2.filletArc");var subQ3=sQuery(id+"F0.wireOp",EDGE,"E1.filletArc");var subQ4=sQuery(id+"F0.wireOp",EDGE,"E0.bottom");var subQ5=sQuery(id+"F0.wireOp",EDGE,"E0.right");var subQ6=sQuery(id+"F0.wireOp",EDGE,"E0.top");var subQ7=sQuery(id+"F0.wireOp",EDGE,"E0.left");Q0=makeQuery(id+"F3.boolean.opBoolean","SPLIT",FACE,{"disambiguationData":[TD([makeQuery(id+"F1.opExtrude","SWEPT_FACE",FACE,{"disambiguationData":[OSD([subQ4])]})])],"derivedFrom":makeQuery(id+"F1.opExtrude","CAP_FACE",FACE,{"disambiguationData":[OSD([subQ4,subQ6,subQ7,subQ5,subQ3,subQ2,subQ1,subQ0])],"isStart":false})});}
            var sketch = newSketch(context, id + "F4", { "sketchPlane" : qUnion([Q0])});
            skLineSegment(sketch, "E731.bottom", {"start": v(0, 182.83) * mm, "end": v(558.8, 182.83) * mm});
            skLineSegment(sketch, "E731.top", {"start": v(0, 71.7) * mm, "end": v(558.8, 71.7) * mm});
            skLineSegment(sketch, "E732.0", {"start": v(0, 12.7) * mm, "end": v(0, 71.7) * mm});
            skArc(sketch, "E733.0", {"start": v(0, 12.7) * mm, "mid": v(3.72, 3.72) * mm, "end": v(12.7, 0) * mm});
            skLineSegment(sketch, "E734.0", {"start": v(12.7, 0) * mm, "end": v(546.1, 0) * mm});
            skArc(sketch, "E735.0", {"start": v(546.1, 0) * mm, "mid": v(555.08, 3.72) * mm, "end": v(558.8, 12.7) * mm});
            skLineSegment(sketch, "E735.1", {"start": v(558.8, 12.7) * mm, "end": v(558.8, 71.7) * mm});
            skLineSegment(sketch, "E736.trimOffspring", {"start": v(0, 182.83) * mm, "end": v(0, 596.9) * mm});
            skLineSegment(sketch, "E737.trimOffspring", {"start": v(558.8, 182.83) * mm, "end": v(558.8, 596.9) * mm});
            skArc(sketch, "E738.0", {"start": v(12.7, 609.6) * mm, "mid": v(3.72, 605.88) * mm, "end": v(0, 596.9) * mm});
            skLineSegment(sketch, "E738.1", {"start": v(12.7, 609.6) * mm, "end": v(546.1, 609.6) * mm});
            skArc(sketch, "E739.0", {"start": v(558.8, 596.9) * mm, "mid": v(555.08, 605.88) * mm, "end": v(546.1, 609.6) * mm});
            skSolve(sketch);
        }
        {
            var Q0;
            Q0=qSketchRegion(id+"F4",true);
            extrude(context, id + "F5", {"entities" : qUnion([Q0]), "operationType" : NewBodyOperationType.REMOVE, "endBound" : BoundingType.THROUGH_ALL, "oppositeDirection" : true, "depth" : 25.4 * mm});
        }
    });
